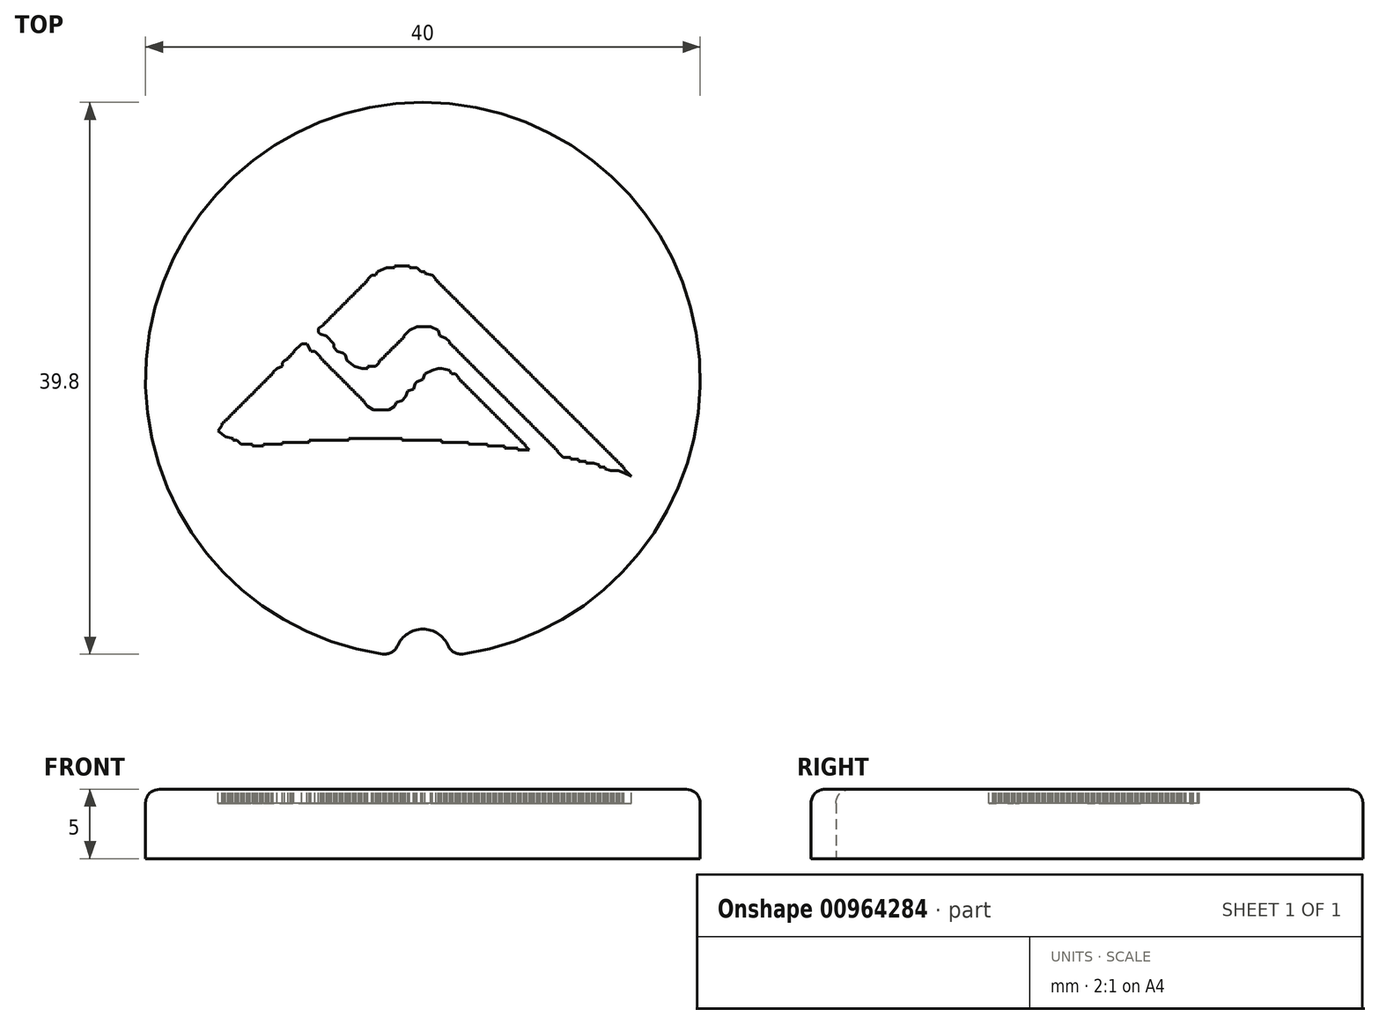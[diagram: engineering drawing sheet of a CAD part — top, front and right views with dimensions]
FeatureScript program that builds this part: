
annotation { "Feature Type Name" : "Feature", "Feature Type Description" : "" }
export const myFeature = defineFeature(function(context is Context, id is Id, definition is map)
    precondition{}
    {
        {
            var Q0;
            Q0=qCreatedBy(makeId("Front.planeOp"),FACE);
            var sketch = newSketch(context, id + "F0", { "sketchPlane" : qUnion([Q0])});
            skLineSegment(sketch, "E0.bottom", {"start": v(0, 0) * mm, "end": v(-20, 0) * mm});
            skLineSegment(sketch, "E0.top", {"start": v(0, 5) * mm, "end": v(-20, 5) * mm});
            skLineSegment(sketch, "E0.left", {"start": v(0, 0) * mm, "end": v(0, 5) * mm});
            skLineSegment(sketch, "E0.right", {"start": v(-20, 0) * mm, "end": v(-20, 5) * mm});
            skSolve(sketch);
        }
        {
            var Q0;
            Q0=qSketchRegion(id+"F0",true);
            var Q1;
            Q1=sQuery(id+"F0.wireOp",EDGE,"E0.left");
            revolve(context, id + "F1", {"surfaceOperationType" : NewSurfaceOperationType.NEW, "entities" : qUnion([Q0]), "axis" : qUnion([Q1]), "revolveType" : RevolveType.FULL});
        }
        {
            var Q0;
            Q0=qCreatedBy(makeId("Top.planeOp"),FACE);
            var sketch = newSketch(context, id + "F2", { "sketchPlane" : qUnion([Q0])});
            skLineSegment(sketch, "E1", {"start": v(0, 0) * mm, "end": v(0, -20) * mm});
            skCircle(sketch, "E2", {"center": v(0, -20) * mm, "radius": 2 * mm});
            skSolve(sketch);
        }
        {
            var Q0;
            Q0=qSketchRegion(id+"F2",true);
            extrude(context, id + "F3", {"entities" : qUnion([Q0]), "operationType" : NewBodyOperationType.REMOVE, "depth" : 25 * mm, "offsetDistance" : 25 * mm});
        }
        {
            var Q0;
            Q0=makeQuery(id+"F1.opRevolve","SWEPT_EDGE",EDGE,{"disambiguationData":[OSD([sQuery(id+"F0.wireOp",EDGE,"E0.top"),sQuery(id+"F0.wireOp",EDGE,"E0.right")])]});
            fillet(context, id + "F4", {"entities" : qUnion([Q0]), "radius" : 1 * mm, "tangentPropagation" : true, "allowEdgeOverflow" : false});
        }
        {
            var Q0;
            Q0=makeQuery(id+"F3.boolean.opBoolean","INTERSECT",EDGE,{"derivedFrom":[makeQuery(id+"F1.opRevolve","SWEPT_FACE",FACE,{"disambiguationData":[OSD([sQuery(id+"F0.wireOp",EDGE,"E0.top")])]}),makeQuery(id+"F3.opExtrude","SWEPT_FACE",FACE,{"disambiguationData":[OSD([sQuery(id+"F2.wireOp",EDGE,"E2")])]})]});
            fillet(context, id + "F5", {"entities" : qUnion([Q0]), "radius" : 1 * mm, "tangentPropagation" : true, "allowEdgeOverflow" : false});
        }
        {
            var Q0;
            Q0=qCreatedBy(makeId("Top.planeOp"),FACE);
            cPlane(context, id + "F6", {"entities" : qUnion([Q0]), "cplaneType" : CPlaneType.OFFSET, "offset" : 5 * mm, "width" : 150 * mm, "height" : 150 * mm});
        }
        {
            var Q0;
            Q0=qCreatedBy(id+"F6.planeOp",FACE);
            var sketch = newSketch(context, id + "F7", { "sketchPlane" : qUnion([Q0])});
            skLineSegment(sketch, "E3", {"start": v(-2.05, 8.2) * mm, "end": v(-2.05, 8.07) * mm});
            skLineSegment(sketch, "E4", {"start": v(-2.05, 8.07) * mm, "end": v(-2.6, 8.07) * mm});
            skLineSegment(sketch, "E5", {"start": v(-2.6, 8.07) * mm, "end": v(-3.28, 7.8) * mm});
            skLineSegment(sketch, "E6", {"start": v(-3.28, 7.8) * mm, "end": v(-3.42, 7.52) * mm});
            skLineSegment(sketch, "E7", {"start": v(-3.42, 7.52) * mm, "end": v(-3.7, 7.52) * mm});
            skLineSegment(sketch, "E8", {"start": v(-3.7, 7.52) * mm, "end": v(-3.97, 7.25) * mm});
            skLineSegment(sketch, "E9", {"start": v(-3.97, 7.25) * mm, "end": v(-3.97, 7.11) * mm});
            skLineSegment(sketch, "E10", {"start": v(-3.97, 7.11) * mm, "end": v(-4.1, 7.11) * mm});
            skLineSegment(sketch, "E11", {"start": v(-4.1, 7.11) * mm, "end": v(-4.1, 6.98) * mm});
            skLineSegment(sketch, "E12", {"start": v(-4.1, 6.98) * mm, "end": v(-4.24, 6.98) * mm});
            skLineSegment(sketch, "E13", {"start": v(-4.24, 6.98) * mm, "end": v(-4.24, 6.84) * mm});
            skLineSegment(sketch, "E14", {"start": v(-4.24, 6.84) * mm, "end": v(-4.38, 6.84) * mm});
            skLineSegment(sketch, "E15", {"start": v(-4.38, 6.84) * mm, "end": v(-4.38, 6.7) * mm});
            skLineSegment(sketch, "E16", {"start": v(-4.38, 6.7) * mm, "end": v(-4.51, 6.7) * mm});
            skLineSegment(sketch, "E17", {"start": v(-4.51, 6.7) * mm, "end": v(-4.51, 6.57) * mm});
            skLineSegment(sketch, "E18", {"start": v(-4.51, 6.57) * mm, "end": v(-4.65, 6.57) * mm});
            skLineSegment(sketch, "E19", {"start": v(-4.65, 6.57) * mm, "end": v(-4.65, 6.43) * mm});
            skLineSegment(sketch, "E20", {"start": v(-4.65, 6.43) * mm, "end": v(-4.79, 6.43) * mm});
            skLineSegment(sketch, "E21", {"start": v(-4.79, 6.43) * mm, "end": v(-4.79, 6.3) * mm});
            skLineSegment(sketch, "E22", {"start": v(-4.79, 6.3) * mm, "end": v(-4.92, 6.3) * mm});
            skLineSegment(sketch, "E23", {"start": v(-4.92, 6.3) * mm, "end": v(-4.92, 6.16) * mm});
            skLineSegment(sketch, "E24", {"start": v(-4.92, 6.16) * mm, "end": v(-5.06, 6.16) * mm});
            skLineSegment(sketch, "E25", {"start": v(-5.06, 6.16) * mm, "end": v(-5.06, 6.02) * mm});
            skLineSegment(sketch, "E26", {"start": v(-5.06, 6.02) * mm, "end": v(-5.2, 6.02) * mm});
            skLineSegment(sketch, "E27", {"start": v(-5.2, 6.02) * mm, "end": v(-5.2, 5.88) * mm});
            skLineSegment(sketch, "E28", {"start": v(-5.2, 5.88) * mm, "end": v(-5.33, 5.88) * mm});
            skLineSegment(sketch, "E29", {"start": v(-5.33, 5.88) * mm, "end": v(-5.33, 5.75) * mm});
            skLineSegment(sketch, "E30", {"start": v(-5.33, 5.75) * mm, "end": v(-5.47, 5.75) * mm});
            skLineSegment(sketch, "E31", {"start": v(-5.47, 5.75) * mm, "end": v(-5.47, 5.6) * mm});
            skLineSegment(sketch, "E32", {"start": v(-5.47, 5.6) * mm, "end": v(-5.6, 5.6) * mm});
            skLineSegment(sketch, "E33", {"start": v(-5.6, 5.6) * mm, "end": v(-5.6, 5.47) * mm});
            skLineSegment(sketch, "E34", {"start": v(-5.6, 5.47) * mm, "end": v(-5.75, 5.47) * mm});
            skLineSegment(sketch, "E35", {"start": v(-5.75, 5.47) * mm, "end": v(-5.75, 5.33) * mm});
            skLineSegment(sketch, "E36", {"start": v(-5.75, 5.33) * mm, "end": v(-5.88, 5.33) * mm});
            skLineSegment(sketch, "E37", {"start": v(-5.88, 5.33) * mm, "end": v(-5.88, 5.2) * mm});
            skLineSegment(sketch, "E38", {"start": v(-5.88, 5.2) * mm, "end": v(-6.02, 5.2) * mm});
            skLineSegment(sketch, "E39", {"start": v(-6.02, 5.2) * mm, "end": v(-6.02, 5.06) * mm});
            skLineSegment(sketch, "E40", {"start": v(-6.02, 5.06) * mm, "end": v(-6.16, 5.06) * mm});
            skLineSegment(sketch, "E41", {"start": v(-6.16, 5.06) * mm, "end": v(-6.16, 4.92) * mm});
            skLineSegment(sketch, "E42", {"start": v(-6.16, 4.92) * mm, "end": v(-6.3, 4.92) * mm});
            skLineSegment(sketch, "E43", {"start": v(-6.3, 4.92) * mm, "end": v(-6.3, 4.79) * mm});
            skLineSegment(sketch, "E44", {"start": v(-6.3, 4.79) * mm, "end": v(-6.43, 4.79) * mm});
            skLineSegment(sketch, "E45", {"start": v(-6.43, 4.79) * mm, "end": v(-6.43, 4.65) * mm});
            skLineSegment(sketch, "E46", {"start": v(-6.43, 4.65) * mm, "end": v(-6.57, 4.65) * mm});
            skLineSegment(sketch, "E47", {"start": v(-6.57, 4.65) * mm, "end": v(-6.57, 4.51) * mm});
            skLineSegment(sketch, "E48", {"start": v(-6.57, 4.51) * mm, "end": v(-6.7, 4.51) * mm});
            skLineSegment(sketch, "E49", {"start": v(-6.7, 4.51) * mm, "end": v(-6.7, 4.38) * mm});
            skLineSegment(sketch, "E50", {"start": v(-6.7, 4.38) * mm, "end": v(-6.84, 4.38) * mm});
            skLineSegment(sketch, "E51", {"start": v(-6.84, 4.38) * mm, "end": v(-6.84, 4.24) * mm});
            skLineSegment(sketch, "E52", {"start": v(-6.84, 4.24) * mm, "end": v(-6.98, 4.24) * mm});
            skLineSegment(sketch, "E53", {"start": v(-6.98, 4.24) * mm, "end": v(-6.98, 4.1) * mm});
            skLineSegment(sketch, "E54", {"start": v(-6.98, 4.1) * mm, "end": v(-7.11, 4.1) * mm});
            skLineSegment(sketch, "E55", {"start": v(-7.11, 4.1) * mm, "end": v(-7.11, 3.97) * mm});
            skLineSegment(sketch, "E56", {"start": v(-7.11, 3.97) * mm, "end": v(-7.52, 3.7) * mm});
            skLineSegment(sketch, "E57", {"start": v(-7.52, 3.7) * mm, "end": v(-7.52, 3.42) * mm});
            skLineSegment(sketch, "E58", {"start": v(-7.52, 3.42) * mm, "end": v(-7.39, 3.28) * mm});
            skLineSegment(sketch, "E59", {"start": v(-7.39, 3.28) * mm, "end": v(-6.98, 3.15) * mm});
            skLineSegment(sketch, "E60", {"start": v(-6.98, 3.15) * mm, "end": v(-6.57, 2.74) * mm});
            skLineSegment(sketch, "E61", {"start": v(-6.57, 2.74) * mm, "end": v(-6.43, 2.6) * mm});
            skLineSegment(sketch, "E62", {"start": v(-6.43, 2.6) * mm, "end": v(-6.43, 2.33) * mm});
            skLineSegment(sketch, "E63", {"start": v(-6.43, 2.33) * mm, "end": v(-6.16, 2.05) * mm});
            skLineSegment(sketch, "E64", {"start": v(-6.16, 2.05) * mm, "end": v(-5.75, 1.92) * mm});
            skLineSegment(sketch, "E65", {"start": v(-5.75, 1.92) * mm, "end": v(-5.6, 1.78) * mm});
            skLineSegment(sketch, "E66", {"start": v(-5.6, 1.78) * mm, "end": v(-5.47, 1.37) * mm});
            skLineSegment(sketch, "E67", {"start": v(-5.47, 1.37) * mm, "end": v(-4.92, 0.96) * mm});
            skLineSegment(sketch, "E68", {"start": v(-4.92, 0.96) * mm, "end": v(-4.38, 0.82) * mm});
            skLineSegment(sketch, "E69", {"start": v(-4.38, 0.82) * mm, "end": v(-3.97, 0.82) * mm});
            skLineSegment(sketch, "E70", {"start": v(-3.97, 0.82) * mm, "end": v(-3.97, 0.96) * mm});
            skLineSegment(sketch, "E71", {"start": v(-3.97, 0.96) * mm, "end": v(-3.42, 0.96) * mm});
            skLineSegment(sketch, "E72", {"start": v(-3.42, 0.96) * mm, "end": v(-3.15, 1.23) * mm});
            skLineSegment(sketch, "E73", {"start": v(-3.15, 1.23) * mm, "end": v(-3.15, 1.37) * mm});
            skLineSegment(sketch, "E74", {"start": v(-3.15, 1.37) * mm, "end": v(-3, 1.37) * mm});
            skLineSegment(sketch, "E75", {"start": v(-3, 1.37) * mm, "end": v(-3, 1.5) * mm});
            skLineSegment(sketch, "E76", {"start": v(-3, 1.5) * mm, "end": v(-2.87, 1.5) * mm});
            skLineSegment(sketch, "E77", {"start": v(-2.87, 1.5) * mm, "end": v(-2.87, 1.64) * mm});
            skLineSegment(sketch, "E78", {"start": v(-2.87, 1.64) * mm, "end": v(-2.74, 1.64) * mm});
            skLineSegment(sketch, "E79", {"start": v(-2.74, 1.64) * mm, "end": v(-2.74, 1.78) * mm});
            skLineSegment(sketch, "E80", {"start": v(-2.74, 1.78) * mm, "end": v(-2.6, 1.78) * mm});
            skLineSegment(sketch, "E81", {"start": v(-2.6, 1.78) * mm, "end": v(-2.6, 1.92) * mm});
            skLineSegment(sketch, "E82", {"start": v(-2.6, 1.92) * mm, "end": v(-2.46, 1.92) * mm});
            skLineSegment(sketch, "E83", {"start": v(-2.46, 1.92) * mm, "end": v(-2.46, 2.05) * mm});
            skLineSegment(sketch, "E84", {"start": v(-2.46, 2.05) * mm, "end": v(-2.33, 2.05) * mm});
            skLineSegment(sketch, "E85", {"start": v(-2.33, 2.05) * mm, "end": v(-2.33, 2.19) * mm});
            skLineSegment(sketch, "E86", {"start": v(-2.33, 2.19) * mm, "end": v(-2.19, 2.19) * mm});
            skLineSegment(sketch, "E87", {"start": v(-2.19, 2.19) * mm, "end": v(-2.19, 2.33) * mm});
            skLineSegment(sketch, "E88", {"start": v(-2.19, 2.33) * mm, "end": v(-2.05, 2.33) * mm});
            skLineSegment(sketch, "E89", {"start": v(-2.05, 2.33) * mm, "end": v(-2.05, 2.46) * mm});
            skLineSegment(sketch, "E90", {"start": v(-2.05, 2.46) * mm, "end": v(-1.92, 2.46) * mm});
            skLineSegment(sketch, "E91", {"start": v(-1.92, 2.46) * mm, "end": v(-1.92, 2.6) * mm});
            skLineSegment(sketch, "E92", {"start": v(-1.92, 2.6) * mm, "end": v(-1.78, 2.6) * mm});
            skLineSegment(sketch, "E93", {"start": v(-1.78, 2.6) * mm, "end": v(-1.78, 2.74) * mm});
            skLineSegment(sketch, "E94", {"start": v(-1.78, 2.74) * mm, "end": v(-1.64, 2.74) * mm});
            skLineSegment(sketch, "E95", {"start": v(-1.64, 2.74) * mm, "end": v(-1.64, 2.87) * mm});
            skLineSegment(sketch, "E96", {"start": v(-1.64, 2.87) * mm, "end": v(-1.5, 2.87) * mm});
            skLineSegment(sketch, "E97", {"start": v(-1.5, 2.87) * mm, "end": v(-1.5, 3) * mm});
            skLineSegment(sketch, "E98", {"start": v(-1.5, 3) * mm, "end": v(-1.37, 3) * mm});
            skLineSegment(sketch, "E99", {"start": v(-1.37, 3) * mm, "end": v(-1.37, 3.15) * mm});
            skLineSegment(sketch, "E100", {"start": v(-1.37, 3.15) * mm, "end": v(-0.96, 3.56) * mm});
            skLineSegment(sketch, "E101", {"start": v(-0.96, 3.56) * mm, "end": v(-0.41, 3.83) * mm});
            skLineSegment(sketch, "E102", {"start": v(-0.41, 3.83) * mm, "end": v(0.55, 3.83) * mm});
            skLineSegment(sketch, "E103", {"start": v(0.55, 3.83) * mm, "end": v(1.1, 3.56) * mm});
            skLineSegment(sketch, "E104", {"start": v(1.1, 3.56) * mm, "end": v(1.23, 3.15) * mm});
            skLineSegment(sketch, "E105", {"start": v(1.23, 3.15) * mm, "end": v(1.64, 3) * mm});
            skLineSegment(sketch, "E106", {"start": v(1.64, 3) * mm, "end": v(1.92, 2.74) * mm});
            skLineSegment(sketch, "E107", {"start": v(1.92, 2.74) * mm, "end": v(1.92, 2.6) * mm});
            skLineSegment(sketch, "E108", {"start": v(1.92, 2.6) * mm, "end": v(2.05, 2.6) * mm});
            skLineSegment(sketch, "E109", {"start": v(2.05, 2.6) * mm, "end": v(2.05, 2.46) * mm});
            skLineSegment(sketch, "E110", {"start": v(2.05, 2.46) * mm, "end": v(2.19, 2.46) * mm});
            skLineSegment(sketch, "E111", {"start": v(2.19, 2.46) * mm, "end": v(2.19, 2.33) * mm});
            skLineSegment(sketch, "E112", {"start": v(2.19, 2.33) * mm, "end": v(2.33, 2.33) * mm});
            skLineSegment(sketch, "E113", {"start": v(2.33, 2.33) * mm, "end": v(2.33, 2.19) * mm});
            skLineSegment(sketch, "E114", {"start": v(2.33, 2.19) * mm, "end": v(2.46, 2.19) * mm});
            skLineSegment(sketch, "E115", {"start": v(2.46, 2.19) * mm, "end": v(2.46, 2.05) * mm});
            skLineSegment(sketch, "E116", {"start": v(2.46, 2.05) * mm, "end": v(2.6, 2.05) * mm});
            skLineSegment(sketch, "E117", {"start": v(2.6, 2.05) * mm, "end": v(2.6, 1.92) * mm});
            skLineSegment(sketch, "E118", {"start": v(2.6, 1.92) * mm, "end": v(2.74, 1.92) * mm});
            skLineSegment(sketch, "E119", {"start": v(2.74, 1.92) * mm, "end": v(2.74, 1.78) * mm});
            skLineSegment(sketch, "E120", {"start": v(2.74, 1.78) * mm, "end": v(2.87, 1.78) * mm});
            skLineSegment(sketch, "E121", {"start": v(2.87, 1.78) * mm, "end": v(2.87, 1.64) * mm});
            skLineSegment(sketch, "E122", {"start": v(2.87, 1.64) * mm, "end": v(3, 1.64) * mm});
            skLineSegment(sketch, "E123", {"start": v(3, 1.64) * mm, "end": v(3, 1.5) * mm});
            skLineSegment(sketch, "E124", {"start": v(3, 1.5) * mm, "end": v(3.15, 1.5) * mm});
            skLineSegment(sketch, "E125", {"start": v(3.15, 1.5) * mm, "end": v(3.15, 1.37) * mm});
            skLineSegment(sketch, "E126", {"start": v(3.15, 1.37) * mm, "end": v(3.28, 1.37) * mm});
            skLineSegment(sketch, "E127", {"start": v(3.28, 1.37) * mm, "end": v(3.28, 1.23) * mm});
            skLineSegment(sketch, "E128", {"start": v(3.28, 1.23) * mm, "end": v(3.42, 1.23) * mm});
            skLineSegment(sketch, "E129", {"start": v(3.42, 1.23) * mm, "end": v(3.42, 1.1) * mm});
            skLineSegment(sketch, "E130", {"start": v(3.42, 1.1) * mm, "end": v(3.56, 1.1) * mm});
            skLineSegment(sketch, "E131", {"start": v(3.56, 1.1) * mm, "end": v(3.56, 0.96) * mm});
            skLineSegment(sketch, "E132", {"start": v(3.56, 0.96) * mm, "end": v(3.7, 0.96) * mm});
            skLineSegment(sketch, "E133", {"start": v(3.7, 0.96) * mm, "end": v(3.7, 0.82) * mm});
            skLineSegment(sketch, "E134", {"start": v(3.7, 0.82) * mm, "end": v(3.83, 0.82) * mm});
            skLineSegment(sketch, "E135", {"start": v(3.83, 0.82) * mm, "end": v(3.83, 0.68) * mm});
            skLineSegment(sketch, "E136", {"start": v(3.83, 0.68) * mm, "end": v(3.97, 0.68) * mm});
            skLineSegment(sketch, "E137", {"start": v(3.97, 0.68) * mm, "end": v(3.97, 0.55) * mm});
            skLineSegment(sketch, "E138", {"start": v(3.97, 0.55) * mm, "end": v(4.1, 0.55) * mm});
            skLineSegment(sketch, "E139", {"start": v(4.1, 0.55) * mm, "end": v(4.1, 0.41) * mm});
            skLineSegment(sketch, "E140", {"start": v(4.1, 0.41) * mm, "end": v(4.24, 0.41) * mm});
            skLineSegment(sketch, "E141", {"start": v(4.24, 0.41) * mm, "end": v(4.24, 0.27) * mm});
            skLineSegment(sketch, "E142", {"start": v(4.24, 0.27) * mm, "end": v(4.38, 0.27) * mm});
            skLineSegment(sketch, "E143", {"start": v(4.38, 0.27) * mm, "end": v(4.38, 0.14) * mm});
            skLineSegment(sketch, "E144", {"start": v(4.38, 0.14) * mm, "end": v(4.51, 0.14) * mm});
            skLineSegment(sketch, "E145", {"start": v(4.51, 0.14) * mm, "end": v(4.51, 0) * mm});
            skLineSegment(sketch, "E146", {"start": v(4.51, 0) * mm, "end": v(4.65, 0) * mm});
            skLineSegment(sketch, "E147", {"start": v(4.65, 0) * mm, "end": v(4.65, -0.14) * mm});
            skLineSegment(sketch, "E148", {"start": v(4.65, -0.14) * mm, "end": v(4.79, -0.14) * mm});
            skLineSegment(sketch, "E149", {"start": v(4.79, -0.14) * mm, "end": v(4.79, -0.27) * mm});
            skLineSegment(sketch, "E150", {"start": v(4.79, -0.27) * mm, "end": v(4.92, -0.27) * mm});
            skLineSegment(sketch, "E151", {"start": v(4.92, -0.27) * mm, "end": v(4.92, -0.41) * mm});
            skLineSegment(sketch, "E152", {"start": v(4.92, -0.41) * mm, "end": v(5.06, -0.41) * mm});
            skLineSegment(sketch, "E153", {"start": v(5.06, -0.41) * mm, "end": v(5.06, -0.55) * mm});
            skLineSegment(sketch, "E154", {"start": v(5.06, -0.55) * mm, "end": v(5.2, -0.55) * mm});
            skLineSegment(sketch, "E155", {"start": v(5.2, -0.55) * mm, "end": v(5.2, -0.68) * mm});
            skLineSegment(sketch, "E156", {"start": v(5.2, -0.68) * mm, "end": v(5.33, -0.68) * mm});
            skLineSegment(sketch, "E157", {"start": v(5.33, -0.68) * mm, "end": v(5.33, -0.82) * mm});
            skLineSegment(sketch, "E158", {"start": v(5.33, -0.82) * mm, "end": v(5.47, -0.82) * mm});
            skLineSegment(sketch, "E159", {"start": v(5.47, -0.82) * mm, "end": v(5.47, -0.96) * mm});
            skLineSegment(sketch, "E160", {"start": v(5.47, -0.96) * mm, "end": v(5.6, -0.96) * mm});
            skLineSegment(sketch, "E161", {"start": v(5.6, -0.96) * mm, "end": v(5.6, -1.1) * mm});
            skLineSegment(sketch, "E162", {"start": v(5.6, -1.1) * mm, "end": v(5.75, -1.1) * mm});
            skLineSegment(sketch, "E163", {"start": v(5.75, -1.1) * mm, "end": v(5.75, -1.23) * mm});
            skLineSegment(sketch, "E164", {"start": v(5.75, -1.23) * mm, "end": v(5.88, -1.23) * mm});
            skLineSegment(sketch, "E165", {"start": v(5.88, -1.23) * mm, "end": v(5.88, -1.37) * mm});
            skLineSegment(sketch, "E166", {"start": v(5.88, -1.37) * mm, "end": v(6.02, -1.37) * mm});
            skLineSegment(sketch, "E167", {"start": v(6.02, -1.37) * mm, "end": v(6.02, -1.5) * mm});
            skLineSegment(sketch, "E168", {"start": v(6.02, -1.5) * mm, "end": v(6.16, -1.5) * mm});
            skLineSegment(sketch, "E169", {"start": v(6.16, -1.5) * mm, "end": v(6.16, -1.64) * mm});
            skLineSegment(sketch, "E170", {"start": v(6.16, -1.64) * mm, "end": v(6.3, -1.64) * mm});
            skLineSegment(sketch, "E171", {"start": v(6.3, -1.64) * mm, "end": v(6.3, -1.78) * mm});
            skLineSegment(sketch, "E172", {"start": v(6.3, -1.78) * mm, "end": v(6.43, -1.78) * mm});
            skLineSegment(sketch, "E173", {"start": v(6.43, -1.78) * mm, "end": v(6.43, -1.92) * mm});
            skLineSegment(sketch, "E174", {"start": v(6.43, -1.92) * mm, "end": v(6.57, -1.92) * mm});
            skLineSegment(sketch, "E175", {"start": v(6.57, -1.92) * mm, "end": v(6.57, -2.05) * mm});
            skLineSegment(sketch, "E176", {"start": v(6.57, -2.05) * mm, "end": v(6.7, -2.05) * mm});
            skLineSegment(sketch, "E177", {"start": v(6.7, -2.05) * mm, "end": v(6.7, -2.19) * mm});
            skLineSegment(sketch, "E178", {"start": v(6.7, -2.19) * mm, "end": v(6.84, -2.19) * mm});
            skLineSegment(sketch, "E179", {"start": v(6.84, -2.19) * mm, "end": v(6.84, -2.33) * mm});
            skLineSegment(sketch, "E180", {"start": v(6.84, -2.33) * mm, "end": v(6.98, -2.33) * mm});
            skLineSegment(sketch, "E181", {"start": v(6.98, -2.33) * mm, "end": v(6.98, -2.46) * mm});
            skLineSegment(sketch, "E182", {"start": v(6.98, -2.46) * mm, "end": v(7.11, -2.46) * mm});
            skLineSegment(sketch, "E183", {"start": v(7.11, -2.46) * mm, "end": v(7.11, -2.6) * mm});
            skLineSegment(sketch, "E184", {"start": v(7.11, -2.6) * mm, "end": v(7.25, -2.6) * mm});
            skLineSegment(sketch, "E185", {"start": v(7.25, -2.6) * mm, "end": v(7.25, -2.74) * mm});
            skLineSegment(sketch, "E186", {"start": v(7.25, -2.74) * mm, "end": v(7.39, -2.74) * mm});
            skLineSegment(sketch, "E187", {"start": v(7.39, -2.74) * mm, "end": v(7.39, -2.87) * mm});
            skLineSegment(sketch, "E188", {"start": v(7.39, -2.87) * mm, "end": v(7.52, -2.87) * mm});
            skLineSegment(sketch, "E189", {"start": v(7.52, -2.87) * mm, "end": v(7.52, -3) * mm});
            skLineSegment(sketch, "E190", {"start": v(7.52, -3) * mm, "end": v(7.66, -3) * mm});
            skLineSegment(sketch, "E191", {"start": v(7.66, -3) * mm, "end": v(7.66, -3.15) * mm});
            skLineSegment(sketch, "E192", {"start": v(7.66, -3.15) * mm, "end": v(7.8, -3.15) * mm});
            skLineSegment(sketch, "E193", {"start": v(7.8, -3.15) * mm, "end": v(7.8, -3.28) * mm});
            skLineSegment(sketch, "E194", {"start": v(7.8, -3.28) * mm, "end": v(7.93, -3.28) * mm});
            skLineSegment(sketch, "E195", {"start": v(7.93, -3.28) * mm, "end": v(7.93, -3.42) * mm});
            skLineSegment(sketch, "E196", {"start": v(7.93, -3.42) * mm, "end": v(8.07, -3.42) * mm});
            skLineSegment(sketch, "E197", {"start": v(8.07, -3.42) * mm, "end": v(8.07, -3.56) * mm});
            skLineSegment(sketch, "E198", {"start": v(8.07, -3.56) * mm, "end": v(8.2, -3.56) * mm});
            skLineSegment(sketch, "E199", {"start": v(8.2, -3.56) * mm, "end": v(8.2, -3.7) * mm});
            skLineSegment(sketch, "E200", {"start": v(8.2, -3.7) * mm, "end": v(8.34, -3.7) * mm});
            skLineSegment(sketch, "E201", {"start": v(8.34, -3.7) * mm, "end": v(8.34, -3.83) * mm});
            skLineSegment(sketch, "E202", {"start": v(8.34, -3.83) * mm, "end": v(8.48, -3.83) * mm});
            skLineSegment(sketch, "E203", {"start": v(8.48, -3.83) * mm, "end": v(8.48, -3.97) * mm});
            skLineSegment(sketch, "E204", {"start": v(8.48, -3.97) * mm, "end": v(8.62, -3.97) * mm});
            skLineSegment(sketch, "E205", {"start": v(8.62, -3.97) * mm, "end": v(8.62, -4.1) * mm});
            skLineSegment(sketch, "E206", {"start": v(8.62, -4.1) * mm, "end": v(8.75, -4.1) * mm});
            skLineSegment(sketch, "E207", {"start": v(8.75, -4.1) * mm, "end": v(8.75, -4.24) * mm});
            skLineSegment(sketch, "E208", {"start": v(8.75, -4.24) * mm, "end": v(8.9, -4.24) * mm});
            skLineSegment(sketch, "E209", {"start": v(8.9, -4.24) * mm, "end": v(8.9, -4.38) * mm});
            skLineSegment(sketch, "E210", {"start": v(8.9, -4.38) * mm, "end": v(9.03, -4.38) * mm});
            skLineSegment(sketch, "E211", {"start": v(9.03, -4.38) * mm, "end": v(9.03, -4.51) * mm});
            skLineSegment(sketch, "E212", {"start": v(9.03, -4.51) * mm, "end": v(9.16, -4.51) * mm});
            skLineSegment(sketch, "E213", {"start": v(9.16, -4.51) * mm, "end": v(9.16, -4.65) * mm});
            skLineSegment(sketch, "E214", {"start": v(9.16, -4.65) * mm, "end": v(9.3, -4.65) * mm});
            skLineSegment(sketch, "E215", {"start": v(9.3, -4.65) * mm, "end": v(9.3, -4.79) * mm});
            skLineSegment(sketch, "E216", {"start": v(9.3, -4.79) * mm, "end": v(9.44, -4.79) * mm});
            skLineSegment(sketch, "E217", {"start": v(9.44, -4.79) * mm, "end": v(9.44, -4.92) * mm});
            skLineSegment(sketch, "E218", {"start": v(9.44, -4.92) * mm, "end": v(9.58, -4.92) * mm});
            skLineSegment(sketch, "E219", {"start": v(9.58, -4.92) * mm, "end": v(9.58, -5.06) * mm});
            skLineSegment(sketch, "E220", {"start": v(9.58, -5.06) * mm, "end": v(9.71, -5.06) * mm});
            skLineSegment(sketch, "E221", {"start": v(9.71, -5.06) * mm, "end": v(9.71, -5.2) * mm});
            skLineSegment(sketch, "E222", {"start": v(9.71, -5.2) * mm, "end": v(10.12, -5.6) * mm});
            skLineSegment(sketch, "E223", {"start": v(10.12, -5.6) * mm, "end": v(10.67, -5.6) * mm});
            skLineSegment(sketch, "E224", {"start": v(10.67, -5.6) * mm, "end": v(10.67, -5.75) * mm});
            skLineSegment(sketch, "E225", {"start": v(10.67, -5.75) * mm, "end": v(11.22, -5.75) * mm});
            skLineSegment(sketch, "E226", {"start": v(11.22, -5.75) * mm, "end": v(11.22, -5.88) * mm});
            skLineSegment(sketch, "E227", {"start": v(11.22, -5.88) * mm, "end": v(11.76, -5.88) * mm});
            skLineSegment(sketch, "E228", {"start": v(11.76, -5.88) * mm, "end": v(11.76, -6.02) * mm});
            skLineSegment(sketch, "E229", {"start": v(11.76, -6.02) * mm, "end": v(12.31, -6.02) * mm});
            skLineSegment(sketch, "E230", {"start": v(12.31, -6.02) * mm, "end": v(12.72, -6.16) * mm});
            skLineSegment(sketch, "E231", {"start": v(12.72, -6.16) * mm, "end": v(12.72, -6.3) * mm});
            skLineSegment(sketch, "E232", {"start": v(12.72, -6.3) * mm, "end": v(13.13, -6.3) * mm});
            skLineSegment(sketch, "E233", {"start": v(13.13, -6.3) * mm, "end": v(13.13, -6.43) * mm});
            skLineSegment(sketch, "E234", {"start": v(13.13, -6.43) * mm, "end": v(13.54, -6.57) * mm});
            skLineSegment(sketch, "E235", {"start": v(13.54, -6.57) * mm, "end": v(14.09, -6.57) * mm});
            skLineSegment(sketch, "E236", {"start": v(14.09, -6.57) * mm, "end": v(14.5, -6.7) * mm});
            skLineSegment(sketch, "E237", {"start": v(14.5, -6.7) * mm, "end": v(15.05, -6.98) * mm});
            skLineSegment(sketch, "E238", {"start": v(15.05, -6.98) * mm, "end": v(14.77, -6.7) * mm});
            skLineSegment(sketch, "E239", {"start": v(14.77, -6.7) * mm, "end": v(14.64, -6.57) * mm});
            skLineSegment(sketch, "E240", {"start": v(14.64, -6.57) * mm, "end": v(14.5, -6.43) * mm});
            skLineSegment(sketch, "E241", {"start": v(14.5, -6.43) * mm, "end": v(14.5, -6.3) * mm});
            skLineSegment(sketch, "E242", {"start": v(14.5, -6.3) * mm, "end": v(14.36, -6.3) * mm});
            skLineSegment(sketch, "E243", {"start": v(14.36, -6.3) * mm, "end": v(14.36, -6.16) * mm});
            skLineSegment(sketch, "E244", {"start": v(14.36, -6.16) * mm, "end": v(14.23, -6.16) * mm});
            skLineSegment(sketch, "E245", {"start": v(14.23, -6.16) * mm, "end": v(14.23, -6.02) * mm});
            skLineSegment(sketch, "E246", {"start": v(14.23, -6.02) * mm, "end": v(14.09, -6.02) * mm});
            skLineSegment(sketch, "E247", {"start": v(14.09, -6.02) * mm, "end": v(14.09, -5.88) * mm});
            skLineSegment(sketch, "E248", {"start": v(14.09, -5.88) * mm, "end": v(13.95, -5.88) * mm});
            skLineSegment(sketch, "E249", {"start": v(13.95, -5.88) * mm, "end": v(13.95, -5.75) * mm});
            skLineSegment(sketch, "E250", {"start": v(13.95, -5.75) * mm, "end": v(13.82, -5.75) * mm});
            skLineSegment(sketch, "E251", {"start": v(13.82, -5.75) * mm, "end": v(13.82, -5.6) * mm});
            skLineSegment(sketch, "E252", {"start": v(13.82, -5.6) * mm, "end": v(13.68, -5.6) * mm});
            skLineSegment(sketch, "E253", {"start": v(13.68, -5.6) * mm, "end": v(13.68, -5.47) * mm});
            skLineSegment(sketch, "E254", {"start": v(13.68, -5.47) * mm, "end": v(13.54, -5.47) * mm});
            skLineSegment(sketch, "E255", {"start": v(13.54, -5.47) * mm, "end": v(13.54, -5.33) * mm});
            skLineSegment(sketch, "E256", {"start": v(13.54, -5.33) * mm, "end": v(13.4, -5.33) * mm});
            skLineSegment(sketch, "E257", {"start": v(13.4, -5.33) * mm, "end": v(13.4, -5.2) * mm});
            skLineSegment(sketch, "E258", {"start": v(13.4, -5.2) * mm, "end": v(13.27, -5.2) * mm});
            skLineSegment(sketch, "E259", {"start": v(13.27, -5.2) * mm, "end": v(13.27, -5.06) * mm});
            skLineSegment(sketch, "E260", {"start": v(13.27, -5.06) * mm, "end": v(13.13, -5.06) * mm});
            skLineSegment(sketch, "E261", {"start": v(13.13, -5.06) * mm, "end": v(13.13, -4.92) * mm});
            skLineSegment(sketch, "E262", {"start": v(13.13, -4.92) * mm, "end": v(13, -4.92) * mm});
            skLineSegment(sketch, "E263", {"start": v(13, -4.92) * mm, "end": v(13, -4.79) * mm});
            skLineSegment(sketch, "E264", {"start": v(13, -4.79) * mm, "end": v(12.86, -4.79) * mm});
            skLineSegment(sketch, "E265", {"start": v(12.86, -4.79) * mm, "end": v(12.86, -4.65) * mm});
            skLineSegment(sketch, "E266", {"start": v(12.86, -4.65) * mm, "end": v(12.72, -4.65) * mm});
            skLineSegment(sketch, "E267", {"start": v(12.72, -4.65) * mm, "end": v(12.72, -4.51) * mm});
            skLineSegment(sketch, "E268", {"start": v(12.72, -4.51) * mm, "end": v(12.58, -4.51) * mm});
            skLineSegment(sketch, "E269", {"start": v(12.58, -4.51) * mm, "end": v(12.58, -4.38) * mm});
            skLineSegment(sketch, "E270", {"start": v(12.58, -4.38) * mm, "end": v(12.45, -4.38) * mm});
            skLineSegment(sketch, "E271", {"start": v(12.45, -4.38) * mm, "end": v(12.45, -4.24) * mm});
            skLineSegment(sketch, "E272", {"start": v(12.45, -4.24) * mm, "end": v(12.31, -4.24) * mm});
            skLineSegment(sketch, "E273", {"start": v(12.31, -4.24) * mm, "end": v(12.31, -4.1) * mm});
            skLineSegment(sketch, "E274", {"start": v(12.31, -4.1) * mm, "end": v(12.17, -4.1) * mm});
            skLineSegment(sketch, "E275", {"start": v(12.17, -4.1) * mm, "end": v(12.17, -3.97) * mm});
            skLineSegment(sketch, "E276", {"start": v(12.17, -3.97) * mm, "end": v(12.04, -3.97) * mm});
            skLineSegment(sketch, "E277", {"start": v(12.04, -3.97) * mm, "end": v(12.04, -3.83) * mm});
            skLineSegment(sketch, "E278", {"start": v(12.04, -3.83) * mm, "end": v(11.9, -3.83) * mm});
            skLineSegment(sketch, "E279", {"start": v(11.9, -3.83) * mm, "end": v(11.9, -3.7) * mm});
            skLineSegment(sketch, "E280", {"start": v(11.9, -3.7) * mm, "end": v(11.76, -3.7) * mm});
            skLineSegment(sketch, "E281", {"start": v(11.76, -3.7) * mm, "end": v(11.76, -3.56) * mm});
            skLineSegment(sketch, "E282", {"start": v(11.76, -3.56) * mm, "end": v(11.63, -3.56) * mm});
            skLineSegment(sketch, "E283", {"start": v(11.63, -3.56) * mm, "end": v(11.63, -3.42) * mm});
            skLineSegment(sketch, "E284", {"start": v(11.63, -3.42) * mm, "end": v(11.5, -3.42) * mm});
            skLineSegment(sketch, "E285", {"start": v(11.5, -3.42) * mm, "end": v(11.5, -3.28) * mm});
            skLineSegment(sketch, "E286", {"start": v(11.5, -3.28) * mm, "end": v(11.35, -3.28) * mm});
            skLineSegment(sketch, "E287", {"start": v(11.35, -3.28) * mm, "end": v(11.35, -3.15) * mm});
            skLineSegment(sketch, "E288", {"start": v(11.35, -3.15) * mm, "end": v(11.22, -3.15) * mm});
            skLineSegment(sketch, "E289", {"start": v(11.22, -3.15) * mm, "end": v(11.22, -3) * mm});
            skLineSegment(sketch, "E290", {"start": v(11.22, -3) * mm, "end": v(11.08, -3) * mm});
            skLineSegment(sketch, "E291", {"start": v(11.08, -3) * mm, "end": v(11.08, -2.87) * mm});
            skLineSegment(sketch, "E292", {"start": v(11.08, -2.87) * mm, "end": v(10.94, -2.87) * mm});
            skLineSegment(sketch, "E293", {"start": v(10.94, -2.87) * mm, "end": v(10.94, -2.74) * mm});
            skLineSegment(sketch, "E294", {"start": v(10.94, -2.74) * mm, "end": v(10.8, -2.74) * mm});
            skLineSegment(sketch, "E295", {"start": v(10.8, -2.74) * mm, "end": v(10.8, -2.6) * mm});
            skLineSegment(sketch, "E296", {"start": v(10.8, -2.6) * mm, "end": v(10.67, -2.6) * mm});
            skLineSegment(sketch, "E297", {"start": v(10.67, -2.6) * mm, "end": v(10.67, -2.46) * mm});
            skLineSegment(sketch, "E298", {"start": v(10.67, -2.46) * mm, "end": v(10.53, -2.46) * mm});
            skLineSegment(sketch, "E299", {"start": v(10.53, -2.46) * mm, "end": v(10.53, -2.33) * mm});
            skLineSegment(sketch, "E300", {"start": v(10.53, -2.33) * mm, "end": v(10.4, -2.33) * mm});
            skLineSegment(sketch, "E301", {"start": v(10.4, -2.33) * mm, "end": v(10.4, -2.19) * mm});
            skLineSegment(sketch, "E302", {"start": v(10.4, -2.19) * mm, "end": v(10.26, -2.19) * mm});
            skLineSegment(sketch, "E303", {"start": v(10.26, -2.19) * mm, "end": v(10.26, -2.05) * mm});
            skLineSegment(sketch, "E304", {"start": v(10.26, -2.05) * mm, "end": v(10.12, -2.05) * mm});
            skLineSegment(sketch, "E305", {"start": v(10.12, -2.05) * mm, "end": v(10.12, -1.92) * mm});
            skLineSegment(sketch, "E306", {"start": v(10.12, -1.92) * mm, "end": v(9.99, -1.92) * mm});
            skLineSegment(sketch, "E307", {"start": v(9.99, -1.92) * mm, "end": v(9.99, -1.78) * mm});
            skLineSegment(sketch, "E308", {"start": v(9.99, -1.78) * mm, "end": v(9.85, -1.78) * mm});
            skLineSegment(sketch, "E309", {"start": v(9.85, -1.78) * mm, "end": v(9.85, -1.64) * mm});
            skLineSegment(sketch, "E310", {"start": v(9.85, -1.64) * mm, "end": v(9.71, -1.64) * mm});
            skLineSegment(sketch, "E311", {"start": v(9.71, -1.64) * mm, "end": v(9.71, -1.5) * mm});
            skLineSegment(sketch, "E312", {"start": v(9.71, -1.5) * mm, "end": v(9.58, -1.5) * mm});
            skLineSegment(sketch, "E313", {"start": v(9.58, -1.5) * mm, "end": v(9.58, -1.37) * mm});
            skLineSegment(sketch, "E314", {"start": v(9.58, -1.37) * mm, "end": v(9.44, -1.37) * mm});
            skLineSegment(sketch, "E315", {"start": v(9.44, -1.37) * mm, "end": v(9.44, -1.23) * mm});
            skLineSegment(sketch, "E316", {"start": v(9.44, -1.23) * mm, "end": v(9.3, -1.23) * mm});
            skLineSegment(sketch, "E317", {"start": v(9.3, -1.23) * mm, "end": v(9.3, -1.1) * mm});
            skLineSegment(sketch, "E318", {"start": v(9.3, -1.1) * mm, "end": v(9.16, -1.1) * mm});
            skLineSegment(sketch, "E319", {"start": v(9.16, -1.1) * mm, "end": v(9.16, -0.96) * mm});
            skLineSegment(sketch, "E320", {"start": v(9.16, -0.96) * mm, "end": v(9.03, -0.96) * mm});
            skLineSegment(sketch, "E321", {"start": v(9.03, -0.96) * mm, "end": v(9.03, -0.82) * mm});
            skLineSegment(sketch, "E322", {"start": v(9.03, -0.82) * mm, "end": v(8.9, -0.82) * mm});
            skLineSegment(sketch, "E323", {"start": v(8.9, -0.82) * mm, "end": v(8.9, -0.68) * mm});
            skLineSegment(sketch, "E324", {"start": v(8.9, -0.68) * mm, "end": v(8.75, -0.68) * mm});
            skLineSegment(sketch, "E325", {"start": v(8.75, -0.68) * mm, "end": v(8.75, -0.55) * mm});
            skLineSegment(sketch, "E326", {"start": v(8.75, -0.55) * mm, "end": v(8.62, -0.55) * mm});
            skLineSegment(sketch, "E327", {"start": v(8.62, -0.55) * mm, "end": v(8.62, -0.41) * mm});
            skLineSegment(sketch, "E328", {"start": v(8.62, -0.41) * mm, "end": v(8.48, -0.41) * mm});
            skLineSegment(sketch, "E329", {"start": v(8.48, -0.41) * mm, "end": v(8.48, -0.27) * mm});
            skLineSegment(sketch, "E330", {"start": v(8.48, -0.27) * mm, "end": v(8.34, -0.27) * mm});
            skLineSegment(sketch, "E331", {"start": v(8.34, -0.27) * mm, "end": v(8.34, -0.14) * mm});
            skLineSegment(sketch, "E332", {"start": v(8.34, -0.14) * mm, "end": v(8.2, -0.14) * mm});
            skLineSegment(sketch, "E333", {"start": v(8.2, -0.14) * mm, "end": v(8.2, 0) * mm});
            skLineSegment(sketch, "E334", {"start": v(8.2, 0) * mm, "end": v(8.07, 0) * mm});
            skLineSegment(sketch, "E335", {"start": v(8.07, 0) * mm, "end": v(8.07, 0.14) * mm});
            skLineSegment(sketch, "E336", {"start": v(8.07, 0.14) * mm, "end": v(7.93, 0.14) * mm});
            skLineSegment(sketch, "E337", {"start": v(7.93, 0.14) * mm, "end": v(7.93, 0.27) * mm});
            skLineSegment(sketch, "E338", {"start": v(7.93, 0.27) * mm, "end": v(7.8, 0.27) * mm});
            skLineSegment(sketch, "E339", {"start": v(7.8, 0.27) * mm, "end": v(7.8, 0.41) * mm});
            skLineSegment(sketch, "E340", {"start": v(7.8, 0.41) * mm, "end": v(7.66, 0.41) * mm});
            skLineSegment(sketch, "E341", {"start": v(7.66, 0.41) * mm, "end": v(7.66, 0.55) * mm});
            skLineSegment(sketch, "E342", {"start": v(7.66, 0.55) * mm, "end": v(7.52, 0.55) * mm});
            skLineSegment(sketch, "E343", {"start": v(7.52, 0.55) * mm, "end": v(7.52, 0.68) * mm});
            skLineSegment(sketch, "E344", {"start": v(7.52, 0.68) * mm, "end": v(7.39, 0.68) * mm});
            skLineSegment(sketch, "E345", {"start": v(7.39, 0.68) * mm, "end": v(7.39, 0.82) * mm});
            skLineSegment(sketch, "E346", {"start": v(7.39, 0.82) * mm, "end": v(7.25, 0.82) * mm});
            skLineSegment(sketch, "E347", {"start": v(7.25, 0.82) * mm, "end": v(7.25, 0.96) * mm});
            skLineSegment(sketch, "E348", {"start": v(7.25, 0.96) * mm, "end": v(7.11, 0.96) * mm});
            skLineSegment(sketch, "E349", {"start": v(7.11, 0.96) * mm, "end": v(7.11, 1.1) * mm});
            skLineSegment(sketch, "E350", {"start": v(7.11, 1.1) * mm, "end": v(6.98, 1.1) * mm});
            skLineSegment(sketch, "E351", {"start": v(6.98, 1.1) * mm, "end": v(6.98, 1.23) * mm});
            skLineSegment(sketch, "E352", {"start": v(6.98, 1.23) * mm, "end": v(6.84, 1.23) * mm});
            skLineSegment(sketch, "E353", {"start": v(6.84, 1.23) * mm, "end": v(6.84, 1.37) * mm});
            skLineSegment(sketch, "E354", {"start": v(6.84, 1.37) * mm, "end": v(6.7, 1.37) * mm});
            skLineSegment(sketch, "E355", {"start": v(6.7, 1.37) * mm, "end": v(6.7, 1.5) * mm});
            skLineSegment(sketch, "E356", {"start": v(6.7, 1.5) * mm, "end": v(6.57, 1.5) * mm});
            skLineSegment(sketch, "E357", {"start": v(6.57, 1.5) * mm, "end": v(6.57, 1.64) * mm});
            skLineSegment(sketch, "E358", {"start": v(6.57, 1.64) * mm, "end": v(6.43, 1.64) * mm});
            skLineSegment(sketch, "E359", {"start": v(6.43, 1.64) * mm, "end": v(6.43, 1.78) * mm});
            skLineSegment(sketch, "E360", {"start": v(6.43, 1.78) * mm, "end": v(6.3, 1.78) * mm});
            skLineSegment(sketch, "E361", {"start": v(6.3, 1.78) * mm, "end": v(6.3, 1.92) * mm});
            skLineSegment(sketch, "E362", {"start": v(6.3, 1.92) * mm, "end": v(6.16, 1.92) * mm});
            skLineSegment(sketch, "E363", {"start": v(6.16, 1.92) * mm, "end": v(6.16, 2.05) * mm});
            skLineSegment(sketch, "E364", {"start": v(6.16, 2.05) * mm, "end": v(6.02, 2.05) * mm});
            skLineSegment(sketch, "E365", {"start": v(6.02, 2.05) * mm, "end": v(6.02, 2.19) * mm});
            skLineSegment(sketch, "E366", {"start": v(6.02, 2.19) * mm, "end": v(5.88, 2.19) * mm});
            skLineSegment(sketch, "E367", {"start": v(5.88, 2.19) * mm, "end": v(5.88, 2.33) * mm});
            skLineSegment(sketch, "E368", {"start": v(5.88, 2.33) * mm, "end": v(5.75, 2.33) * mm});
            skLineSegment(sketch, "E369", {"start": v(5.75, 2.33) * mm, "end": v(5.75, 2.46) * mm});
            skLineSegment(sketch, "E370", {"start": v(5.75, 2.46) * mm, "end": v(5.6, 2.46) * mm});
            skLineSegment(sketch, "E371", {"start": v(5.6, 2.46) * mm, "end": v(5.6, 2.6) * mm});
            skLineSegment(sketch, "E372", {"start": v(5.6, 2.6) * mm, "end": v(5.47, 2.6) * mm});
            skLineSegment(sketch, "E373", {"start": v(5.47, 2.6) * mm, "end": v(5.47, 2.74) * mm});
            skLineSegment(sketch, "E374", {"start": v(5.47, 2.74) * mm, "end": v(5.33, 2.74) * mm});
            skLineSegment(sketch, "E375", {"start": v(5.33, 2.74) * mm, "end": v(5.33, 2.87) * mm});
            skLineSegment(sketch, "E376", {"start": v(5.33, 2.87) * mm, "end": v(5.2, 2.87) * mm});
            skLineSegment(sketch, "E377", {"start": v(5.2, 2.87) * mm, "end": v(5.2, 3) * mm});
            skLineSegment(sketch, "E378", {"start": v(5.2, 3) * mm, "end": v(5.06, 3) * mm});
            skLineSegment(sketch, "E379", {"start": v(5.06, 3) * mm, "end": v(5.06, 3.15) * mm});
            skLineSegment(sketch, "E380", {"start": v(5.06, 3.15) * mm, "end": v(4.92, 3.15) * mm});
            skLineSegment(sketch, "E381", {"start": v(4.92, 3.15) * mm, "end": v(4.92, 3.28) * mm});
            skLineSegment(sketch, "E382", {"start": v(4.92, 3.28) * mm, "end": v(4.79, 3.28) * mm});
            skLineSegment(sketch, "E383", {"start": v(4.79, 3.28) * mm, "end": v(4.79, 3.42) * mm});
            skLineSegment(sketch, "E384", {"start": v(4.79, 3.42) * mm, "end": v(4.65, 3.42) * mm});
            skLineSegment(sketch, "E385", {"start": v(4.65, 3.42) * mm, "end": v(4.65, 3.56) * mm});
            skLineSegment(sketch, "E386", {"start": v(4.65, 3.56) * mm, "end": v(4.51, 3.56) * mm});
            skLineSegment(sketch, "E387", {"start": v(4.51, 3.56) * mm, "end": v(4.51, 3.7) * mm});
            skLineSegment(sketch, "E388", {"start": v(4.51, 3.7) * mm, "end": v(4.38, 3.7) * mm});
            skLineSegment(sketch, "E389", {"start": v(4.38, 3.7) * mm, "end": v(4.38, 3.83) * mm});
            skLineSegment(sketch, "E390", {"start": v(4.38, 3.83) * mm, "end": v(4.24, 3.83) * mm});
            skLineSegment(sketch, "E391", {"start": v(4.24, 3.83) * mm, "end": v(4.24, 3.97) * mm});
            skLineSegment(sketch, "E392", {"start": v(4.24, 3.97) * mm, "end": v(4.1, 3.97) * mm});
            skLineSegment(sketch, "E393", {"start": v(4.1, 3.97) * mm, "end": v(4.1, 4.1) * mm});
            skLineSegment(sketch, "E394", {"start": v(4.1, 4.1) * mm, "end": v(3.97, 4.1) * mm});
            skLineSegment(sketch, "E395", {"start": v(3.97, 4.1) * mm, "end": v(3.97, 4.24) * mm});
            skLineSegment(sketch, "E396", {"start": v(3.97, 4.24) * mm, "end": v(3.83, 4.24) * mm});
            skLineSegment(sketch, "E397", {"start": v(3.83, 4.24) * mm, "end": v(3.83, 4.38) * mm});
            skLineSegment(sketch, "E398", {"start": v(3.83, 4.38) * mm, "end": v(3.7, 4.38) * mm});
            skLineSegment(sketch, "E399", {"start": v(3.7, 4.38) * mm, "end": v(3.7, 4.51) * mm});
            skLineSegment(sketch, "E400", {"start": v(3.7, 4.51) * mm, "end": v(3.56, 4.51) * mm});
            skLineSegment(sketch, "E401", {"start": v(3.56, 4.51) * mm, "end": v(3.56, 4.65) * mm});
            skLineSegment(sketch, "E402", {"start": v(3.56, 4.65) * mm, "end": v(3.42, 4.65) * mm});
            skLineSegment(sketch, "E403", {"start": v(3.42, 4.65) * mm, "end": v(3.42, 4.79) * mm});
            skLineSegment(sketch, "E404", {"start": v(3.42, 4.79) * mm, "end": v(3.28, 4.79) * mm});
            skLineSegment(sketch, "E405", {"start": v(3.28, 4.79) * mm, "end": v(3.28, 4.92) * mm});
            skLineSegment(sketch, "E406", {"start": v(3.28, 4.92) * mm, "end": v(3.15, 4.92) * mm});
            skLineSegment(sketch, "E407", {"start": v(3.15, 4.92) * mm, "end": v(3.15, 5.06) * mm});
            skLineSegment(sketch, "E408", {"start": v(3.15, 5.06) * mm, "end": v(3, 5.06) * mm});
            skLineSegment(sketch, "E409", {"start": v(3, 5.06) * mm, "end": v(3, 5.2) * mm});
            skLineSegment(sketch, "E410", {"start": v(3, 5.2) * mm, "end": v(2.87, 5.2) * mm});
            skLineSegment(sketch, "E411", {"start": v(2.87, 5.2) * mm, "end": v(2.87, 5.33) * mm});
            skLineSegment(sketch, "E412", {"start": v(2.87, 5.33) * mm, "end": v(2.74, 5.33) * mm});
            skLineSegment(sketch, "E413", {"start": v(2.74, 5.33) * mm, "end": v(2.74, 5.47) * mm});
            skLineSegment(sketch, "E414", {"start": v(2.74, 5.47) * mm, "end": v(2.6, 5.47) * mm});
            skLineSegment(sketch, "E415", {"start": v(2.6, 5.47) * mm, "end": v(2.6, 5.6) * mm});
            skLineSegment(sketch, "E416", {"start": v(2.6, 5.6) * mm, "end": v(2.46, 5.6) * mm});
            skLineSegment(sketch, "E417", {"start": v(2.46, 5.6) * mm, "end": v(2.46, 5.75) * mm});
            skLineSegment(sketch, "E418", {"start": v(2.46, 5.75) * mm, "end": v(2.33, 5.75) * mm});
            skLineSegment(sketch, "E419", {"start": v(2.33, 5.75) * mm, "end": v(2.33, 5.88) * mm});
            skLineSegment(sketch, "E420", {"start": v(2.33, 5.88) * mm, "end": v(2.19, 5.88) * mm});
            skLineSegment(sketch, "E421", {"start": v(2.19, 5.88) * mm, "end": v(2.19, 6.02) * mm});
            skLineSegment(sketch, "E422", {"start": v(2.19, 6.02) * mm, "end": v(2.05, 6.02) * mm});
            skLineSegment(sketch, "E423", {"start": v(2.05, 6.02) * mm, "end": v(2.05, 6.16) * mm});
            skLineSegment(sketch, "E424", {"start": v(2.05, 6.16) * mm, "end": v(1.92, 6.16) * mm});
            skLineSegment(sketch, "E425", {"start": v(1.92, 6.16) * mm, "end": v(1.92, 6.3) * mm});
            skLineSegment(sketch, "E426", {"start": v(1.92, 6.3) * mm, "end": v(1.78, 6.3) * mm});
            skLineSegment(sketch, "E427", {"start": v(1.78, 6.3) * mm, "end": v(1.78, 6.43) * mm});
            skLineSegment(sketch, "E428", {"start": v(1.78, 6.43) * mm, "end": v(1.64, 6.43) * mm});
            skLineSegment(sketch, "E429", {"start": v(1.64, 6.43) * mm, "end": v(1.64, 6.57) * mm});
            skLineSegment(sketch, "E430", {"start": v(1.64, 6.57) * mm, "end": v(1.5, 6.57) * mm});
            skLineSegment(sketch, "E431", {"start": v(1.5, 6.57) * mm, "end": v(1.5, 6.7) * mm});
            skLineSegment(sketch, "E432", {"start": v(1.5, 6.7) * mm, "end": v(1.37, 6.7) * mm});
            skLineSegment(sketch, "E433", {"start": v(1.37, 6.7) * mm, "end": v(1.37, 6.84) * mm});
            skLineSegment(sketch, "E434", {"start": v(1.37, 6.84) * mm, "end": v(1.23, 6.84) * mm});
            skLineSegment(sketch, "E435", {"start": v(1.23, 6.84) * mm, "end": v(1.23, 6.98) * mm});
            skLineSegment(sketch, "E436", {"start": v(1.23, 6.98) * mm, "end": v(1.1, 6.98) * mm});
            skLineSegment(sketch, "E437", {"start": v(1.1, 6.98) * mm, "end": v(1.1, 7.11) * mm});
            skLineSegment(sketch, "E438", {"start": v(1.1, 7.11) * mm, "end": v(0.96, 7.11) * mm});
            skLineSegment(sketch, "E439", {"start": v(0.96, 7.11) * mm, "end": v(0.96, 7.25) * mm});
            skLineSegment(sketch, "E440", {"start": v(0.96, 7.25) * mm, "end": v(0.68, 7.52) * mm});
            skLineSegment(sketch, "E441", {"start": v(0.68, 7.52) * mm, "end": v(0.14, 7.66) * mm});
            skLineSegment(sketch, "E442", {"start": v(0.14, 7.66) * mm, "end": v(0.14, 7.8) * mm});
            skLineSegment(sketch, "E443", {"start": v(0.14, 7.8) * mm, "end": v(-0.14, 7.8) * mm});
            skLineSegment(sketch, "E444", {"start": v(-0.14, 7.8) * mm, "end": v(-0.41, 8.07) * mm});
            skLineSegment(sketch, "E445", {"start": v(-0.41, 8.07) * mm, "end": v(-0.96, 8.07) * mm});
            skLineSegment(sketch, "E446", {"start": v(-0.96, 8.07) * mm, "end": v(-0.96, 8.2) * mm});
            skLineSegment(sketch, "E447", {"start": v(-0.96, 8.2) * mm, "end": v(-2.05, 8.2) * mm});
            skLineSegment(sketch, "E448", {"start": v(-8.75, 2.6) * mm, "end": v(-9.03, 2.33) * mm});
            skLineSegment(sketch, "E449", {"start": v(-9.03, 2.33) * mm, "end": v(-9.16, 2.19) * mm});
            skLineSegment(sketch, "E450", {"start": v(-9.16, 2.19) * mm, "end": v(-9.3, 2.05) * mm});
            skLineSegment(sketch, "E451", {"start": v(-9.3, 2.05) * mm, "end": v(-9.3, 1.92) * mm});
            skLineSegment(sketch, "E452", {"start": v(-9.3, 1.92) * mm, "end": v(-9.44, 1.92) * mm});
            skLineSegment(sketch, "E453", {"start": v(-9.44, 1.92) * mm, "end": v(-9.44, 1.78) * mm});
            skLineSegment(sketch, "E454", {"start": v(-9.44, 1.78) * mm, "end": v(-9.58, 1.78) * mm});
            skLineSegment(sketch, "E455", {"start": v(-9.58, 1.78) * mm, "end": v(-9.58, 1.64) * mm});
            skLineSegment(sketch, "E456", {"start": v(-9.58, 1.64) * mm, "end": v(-9.71, 1.64) * mm});
            skLineSegment(sketch, "E457", {"start": v(-9.71, 1.64) * mm, "end": v(-9.71, 1.5) * mm});
            skLineSegment(sketch, "E458", {"start": v(-9.71, 1.5) * mm, "end": v(-9.99, 1.37) * mm});
            skLineSegment(sketch, "E459", {"start": v(-9.99, 1.37) * mm, "end": v(-10.12, 1.23) * mm});
            skLineSegment(sketch, "E460", {"start": v(-10.12, 1.23) * mm, "end": v(-10.12, 0.96) * mm});
            skLineSegment(sketch, "E461", {"start": v(-10.12, 0.96) * mm, "end": v(-10.53, 0.82) * mm});
            skLineSegment(sketch, "E462", {"start": v(-10.53, 0.82) * mm, "end": v(-10.8, 0.55) * mm});
            skLineSegment(sketch, "E463", {"start": v(-10.8, 0.55) * mm, "end": v(-10.8, 0.41) * mm});
            skLineSegment(sketch, "E464", {"start": v(-10.8, 0.41) * mm, "end": v(-10.94, 0.41) * mm});
            skLineSegment(sketch, "E465", {"start": v(-10.94, 0.41) * mm, "end": v(-10.94, 0.27) * mm});
            skLineSegment(sketch, "E466", {"start": v(-10.94, 0.27) * mm, "end": v(-11.08, 0.27) * mm});
            skLineSegment(sketch, "E467", {"start": v(-11.08, 0.27) * mm, "end": v(-11.08, 0.14) * mm});
            skLineSegment(sketch, "E468", {"start": v(-11.08, 0.14) * mm, "end": v(-11.22, 0.14) * mm});
            skLineSegment(sketch, "E469", {"start": v(-11.22, 0.14) * mm, "end": v(-11.22, 0) * mm});
            skLineSegment(sketch, "E470", {"start": v(-11.22, 0) * mm, "end": v(-11.35, 0) * mm});
            skLineSegment(sketch, "E471", {"start": v(-11.35, 0) * mm, "end": v(-11.35, -0.14) * mm});
            skLineSegment(sketch, "E472", {"start": v(-11.35, -0.14) * mm, "end": v(-11.5, -0.14) * mm});
            skLineSegment(sketch, "E473", {"start": v(-11.5, -0.14) * mm, "end": v(-11.5, -0.27) * mm});
            skLineSegment(sketch, "E474", {"start": v(-11.5, -0.27) * mm, "end": v(-11.63, -0.27) * mm});
            skLineSegment(sketch, "E475", {"start": v(-11.63, -0.27) * mm, "end": v(-11.63, -0.41) * mm});
            skLineSegment(sketch, "E476", {"start": v(-11.63, -0.41) * mm, "end": v(-11.76, -0.41) * mm});
            skLineSegment(sketch, "E477", {"start": v(-11.76, -0.41) * mm, "end": v(-11.76, -0.55) * mm});
            skLineSegment(sketch, "E478", {"start": v(-11.76, -0.55) * mm, "end": v(-11.9, -0.55) * mm});
            skLineSegment(sketch, "E479", {"start": v(-11.9, -0.55) * mm, "end": v(-11.9, -0.68) * mm});
            skLineSegment(sketch, "E480", {"start": v(-11.9, -0.68) * mm, "end": v(-12.04, -0.68) * mm});
            skLineSegment(sketch, "E481", {"start": v(-12.04, -0.68) * mm, "end": v(-12.04, -0.82) * mm});
            skLineSegment(sketch, "E482", {"start": v(-12.04, -0.82) * mm, "end": v(-12.17, -0.82) * mm});
            skLineSegment(sketch, "E483", {"start": v(-12.17, -0.82) * mm, "end": v(-12.17, -0.96) * mm});
            skLineSegment(sketch, "E484", {"start": v(-12.17, -0.96) * mm, "end": v(-12.31, -0.96) * mm});
            skLineSegment(sketch, "E485", {"start": v(-12.31, -0.96) * mm, "end": v(-12.31, -1.1) * mm});
            skLineSegment(sketch, "E486", {"start": v(-12.31, -1.1) * mm, "end": v(-12.45, -1.1) * mm});
            skLineSegment(sketch, "E487", {"start": v(-12.45, -1.1) * mm, "end": v(-12.45, -1.23) * mm});
            skLineSegment(sketch, "E488", {"start": v(-12.45, -1.23) * mm, "end": v(-12.58, -1.23) * mm});
            skLineSegment(sketch, "E489", {"start": v(-12.58, -1.23) * mm, "end": v(-12.58, -1.37) * mm});
            skLineSegment(sketch, "E490", {"start": v(-12.58, -1.37) * mm, "end": v(-12.72, -1.37) * mm});
            skLineSegment(sketch, "E491", {"start": v(-12.72, -1.37) * mm, "end": v(-12.72, -1.5) * mm});
            skLineSegment(sketch, "E492", {"start": v(-12.72, -1.5) * mm, "end": v(-12.86, -1.5) * mm});
            skLineSegment(sketch, "E493", {"start": v(-12.86, -1.5) * mm, "end": v(-12.86, -1.64) * mm});
            skLineSegment(sketch, "E494", {"start": v(-12.86, -1.64) * mm, "end": v(-13, -1.64) * mm});
            skLineSegment(sketch, "E495", {"start": v(-13, -1.64) * mm, "end": v(-13, -1.78) * mm});
            skLineSegment(sketch, "E496", {"start": v(-13, -1.78) * mm, "end": v(-13.13, -1.78) * mm});
            skLineSegment(sketch, "E497", {"start": v(-13.13, -1.78) * mm, "end": v(-13.13, -1.92) * mm});
            skLineSegment(sketch, "E498", {"start": v(-13.13, -1.92) * mm, "end": v(-13.27, -1.92) * mm});
            skLineSegment(sketch, "E499", {"start": v(-13.27, -1.92) * mm, "end": v(-13.27, -2.05) * mm});
            skLineSegment(sketch, "E500", {"start": v(-13.27, -2.05) * mm, "end": v(-13.4, -2.05) * mm});
            skLineSegment(sketch, "E501", {"start": v(-13.4, -2.05) * mm, "end": v(-13.4, -2.19) * mm});
            skLineSegment(sketch, "E502", {"start": v(-13.4, -2.19) * mm, "end": v(-13.54, -2.19) * mm});
            skLineSegment(sketch, "E503", {"start": v(-13.54, -2.19) * mm, "end": v(-13.54, -2.33) * mm});
            skLineSegment(sketch, "E504", {"start": v(-13.54, -2.33) * mm, "end": v(-13.68, -2.33) * mm});
            skLineSegment(sketch, "E505", {"start": v(-13.68, -2.33) * mm, "end": v(-13.68, -2.46) * mm});
            skLineSegment(sketch, "E506", {"start": v(-13.68, -2.46) * mm, "end": v(-13.82, -2.46) * mm});
            skLineSegment(sketch, "E507", {"start": v(-13.82, -2.46) * mm, "end": v(-13.82, -2.6) * mm});
            skLineSegment(sketch, "E508", {"start": v(-13.82, -2.6) * mm, "end": v(-13.95, -2.6) * mm});
            skLineSegment(sketch, "E509", {"start": v(-13.95, -2.6) * mm, "end": v(-13.95, -2.74) * mm});
            skLineSegment(sketch, "E510", {"start": v(-13.95, -2.74) * mm, "end": v(-14.09, -2.74) * mm});
            skLineSegment(sketch, "E511", {"start": v(-14.09, -2.74) * mm, "end": v(-14.09, -2.87) * mm});
            skLineSegment(sketch, "E512", {"start": v(-14.09, -2.87) * mm, "end": v(-14.23, -2.87) * mm});
            skLineSegment(sketch, "E513", {"start": v(-14.23, -2.87) * mm, "end": v(-14.23, -3) * mm});
            skLineSegment(sketch, "E514", {"start": v(-14.23, -3) * mm, "end": v(-14.36, -3) * mm});
            skLineSegment(sketch, "E515", {"start": v(-14.36, -3) * mm, "end": v(-14.36, -3.15) * mm});
            skLineSegment(sketch, "E516", {"start": v(-14.36, -3.15) * mm, "end": v(-14.5, -3.15) * mm});
            skLineSegment(sketch, "E517", {"start": v(-14.5, -3.15) * mm, "end": v(-14.5, -3.28) * mm});
            skLineSegment(sketch, "E518", {"start": v(-14.5, -3.28) * mm, "end": v(-14.77, -3.7) * mm});
            skLineSegment(sketch, "E519", {"start": v(-14.77, -3.7) * mm, "end": v(-14.23, -4.1) * mm});
            skLineSegment(sketch, "E520", {"start": v(-14.23, -4.1) * mm, "end": v(-13.68, -4.24) * mm});
            skLineSegment(sketch, "E521", {"start": v(-13.68, -4.24) * mm, "end": v(-13.68, -4.38) * mm});
            skLineSegment(sketch, "E522", {"start": v(-13.68, -4.38) * mm, "end": v(-13.4, -4.38) * mm});
            skLineSegment(sketch, "E523", {"start": v(-13.4, -4.38) * mm, "end": v(-13.13, -4.65) * mm});
            skLineSegment(sketch, "E524", {"start": v(-13.13, -4.65) * mm, "end": v(-12.31, -4.65) * mm});
            skLineSegment(sketch, "E525", {"start": v(-12.31, -4.65) * mm, "end": v(-12.31, -4.79) * mm});
            skLineSegment(sketch, "E526", {"start": v(-12.31, -4.79) * mm, "end": v(-11.5, -4.79) * mm});
            skLineSegment(sketch, "E527", {"start": v(-11.5, -4.79) * mm, "end": v(-11.5, -4.65) * mm});
            skLineSegment(sketch, "E528", {"start": v(-11.5, -4.65) * mm, "end": v(-11.08, -4.65) * mm});
            skLineSegment(sketch, "E529", {"start": v(-11.08, -4.65) * mm, "end": v(-10.12, -4.65) * mm});
            skLineSegment(sketch, "E530", {"start": v(-10.12, -4.65) * mm, "end": v(-10.12, -4.51) * mm});
            skLineSegment(sketch, "E531", {"start": v(-10.12, -4.51) * mm, "end": v(-9.71, -4.51) * mm});
            skLineSegment(sketch, "E532", {"start": v(-9.71, -4.51) * mm, "end": v(-9.16, -4.51) * mm});
            skLineSegment(sketch, "E533", {"start": v(-9.16, -4.51) * mm, "end": v(-9.03, -4.51) * mm});
            skLineSegment(sketch, "E534", {"start": v(-9.03, -4.51) * mm, "end": v(-8.9, -4.51) * mm});
            skLineSegment(sketch, "E535", {"start": v(-8.9, -4.51) * mm, "end": v(-8.75, -4.51) * mm});
            skLineSegment(sketch, "E536", {"start": v(-8.75, -4.51) * mm, "end": v(-8.2, -4.51) * mm});
            skLineSegment(sketch, "E537", {"start": v(-8.2, -4.51) * mm, "end": v(-8.2, -4.38) * mm});
            skLineSegment(sketch, "E538", {"start": v(-8.2, -4.38) * mm, "end": v(-7.8, -4.38) * mm});
            skLineSegment(sketch, "E539", {"start": v(-7.8, -4.38) * mm, "end": v(-7.25, -4.38) * mm});
            skLineSegment(sketch, "E540", {"start": v(-7.25, -4.38) * mm, "end": v(-7.11, -4.38) * mm});
            skLineSegment(sketch, "E541", {"start": v(-7.11, -4.38) * mm, "end": v(-6.98, -4.38) * mm});
            skLineSegment(sketch, "E542", {"start": v(-6.98, -4.38) * mm, "end": v(-6.84, -4.38) * mm});
            skLineSegment(sketch, "E543", {"start": v(-6.84, -4.38) * mm, "end": v(-6.7, -4.38) * mm});
            skLineSegment(sketch, "E544", {"start": v(-6.7, -4.38) * mm, "end": v(-6.57, -4.38) * mm});
            skLineSegment(sketch, "E545", {"start": v(-6.57, -4.38) * mm, "end": v(-6.43, -4.38) * mm});
            skLineSegment(sketch, "E546", {"start": v(-6.43, -4.38) * mm, "end": v(-6.3, -4.38) * mm});
            skLineSegment(sketch, "E547", {"start": v(-6.3, -4.38) * mm, "end": v(-5.33, -4.38) * mm});
            skLineSegment(sketch, "E548", {"start": v(-5.33, -4.38) * mm, "end": v(-5.33, -4.24) * mm});
            skLineSegment(sketch, "E549", {"start": v(-5.33, -4.24) * mm, "end": v(-4.92, -4.24) * mm});
            skLineSegment(sketch, "E550", {"start": v(-4.92, -4.24) * mm, "end": v(-4.38, -4.24) * mm});
            skLineSegment(sketch, "E551", {"start": v(-4.38, -4.24) * mm, "end": v(-4.24, -4.24) * mm});
            skLineSegment(sketch, "E552", {"start": v(-4.24, -4.24) * mm, "end": v(-4.1, -4.24) * mm});
            skLineSegment(sketch, "E553", {"start": v(-4.1, -4.24) * mm, "end": v(-3.97, -4.24) * mm});
            skLineSegment(sketch, "E554", {"start": v(-3.97, -4.24) * mm, "end": v(-3.83, -4.24) * mm});
            skLineSegment(sketch, "E555", {"start": v(-3.83, -4.24) * mm, "end": v(-3.7, -4.24) * mm});
            skLineSegment(sketch, "E556", {"start": v(-3.7, -4.24) * mm, "end": v(-3.56, -4.24) * mm});
            skLineSegment(sketch, "E557", {"start": v(-3.56, -4.24) * mm, "end": v(-3.42, -4.24) * mm});
            skLineSegment(sketch, "E558", {"start": v(-3.42, -4.24) * mm, "end": v(-3.28, -4.24) * mm});
            skLineSegment(sketch, "E559", {"start": v(-3.28, -4.24) * mm, "end": v(-3.15, -4.24) * mm});
            skLineSegment(sketch, "E560", {"start": v(-3.15, -4.24) * mm, "end": v(-3, -4.24) * mm});
            skLineSegment(sketch, "E561", {"start": v(-3, -4.24) * mm, "end": v(-2.87, -4.24) * mm});
            skLineSegment(sketch, "E562", {"start": v(-2.87, -4.24) * mm, "end": v(-2.74, -4.24) * mm});
            skLineSegment(sketch, "E563", {"start": v(-2.74, -4.24) * mm, "end": v(-2.6, -4.24) * mm});
            skLineSegment(sketch, "E564", {"start": v(-2.6, -4.24) * mm, "end": v(-2.46, -4.24) * mm});
            skLineSegment(sketch, "E565", {"start": v(-2.46, -4.24) * mm, "end": v(-2.33, -4.24) * mm});
            skLineSegment(sketch, "E566", {"start": v(-2.33, -4.24) * mm, "end": v(-1.5, -4.24) * mm});
            skLineSegment(sketch, "E567", {"start": v(-1.5, -4.24) * mm, "end": v(-1.5, -4.38) * mm});
            skLineSegment(sketch, "E568", {"start": v(-1.5, -4.38) * mm, "end": v(-1.1, -4.38) * mm});
            skLineSegment(sketch, "E569", {"start": v(-1.1, -4.38) * mm, "end": v(-0.55, -4.38) * mm});
            skLineSegment(sketch, "E570", {"start": v(-0.55, -4.38) * mm, "end": v(-0.41, -4.38) * mm});
            skLineSegment(sketch, "E571", {"start": v(-0.41, -4.38) * mm, "end": v(-0.27, -4.38) * mm});
            skLineSegment(sketch, "E572", {"start": v(-0.27, -4.38) * mm, "end": v(-0.14, -4.38) * mm});
            skLineSegment(sketch, "E573", {"start": v(-0.14, -4.38) * mm, "end": v(0, -4.38) * mm});
            skLineSegment(sketch, "E574", {"start": v(0, -4.38) * mm, "end": v(0.14, -4.38) * mm});
            skLineSegment(sketch, "E575", {"start": v(0.14, -4.38) * mm, "end": v(0.27, -4.38) * mm});
            skLineSegment(sketch, "E576", {"start": v(0.27, -4.38) * mm, "end": v(0.41, -4.38) * mm});
            skLineSegment(sketch, "E577", {"start": v(0.41, -4.38) * mm, "end": v(1.37, -4.38) * mm});
            skLineSegment(sketch, "E578", {"start": v(1.37, -4.38) * mm, "end": v(1.37, -4.51) * mm});
            skLineSegment(sketch, "E579", {"start": v(1.37, -4.51) * mm, "end": v(1.78, -4.51) * mm});
            skLineSegment(sketch, "E580", {"start": v(1.78, -4.51) * mm, "end": v(2.33, -4.51) * mm});
            skLineSegment(sketch, "E581", {"start": v(2.33, -4.51) * mm, "end": v(2.46, -4.51) * mm});
            skLineSegment(sketch, "E582", {"start": v(2.46, -4.51) * mm, "end": v(2.6, -4.51) * mm});
            skLineSegment(sketch, "E583", {"start": v(2.6, -4.51) * mm, "end": v(2.74, -4.51) * mm});
            skLineSegment(sketch, "E584", {"start": v(2.74, -4.51) * mm, "end": v(3.28, -4.51) * mm});
            skLineSegment(sketch, "E585", {"start": v(3.28, -4.51) * mm, "end": v(3.28, -4.65) * mm});
            skLineSegment(sketch, "E586", {"start": v(3.28, -4.65) * mm, "end": v(3.7, -4.65) * mm});
            skLineSegment(sketch, "E587", {"start": v(3.7, -4.65) * mm, "end": v(4.65, -4.65) * mm});
            skLineSegment(sketch, "E588", {"start": v(4.65, -4.65) * mm, "end": v(4.65, -4.79) * mm});
            skLineSegment(sketch, "E589", {"start": v(4.65, -4.79) * mm, "end": v(5.06, -4.79) * mm});
            skLineSegment(sketch, "E590", {"start": v(5.06, -4.79) * mm, "end": v(5.47, -4.79) * mm});
            skLineSegment(sketch, "E591", {"start": v(5.47, -4.79) * mm, "end": v(5.88, -4.79) * mm});
            skLineSegment(sketch, "E592", {"start": v(5.88, -4.79) * mm, "end": v(5.88, -4.92) * mm});
            skLineSegment(sketch, "E593", {"start": v(5.88, -4.92) * mm, "end": v(6.84, -4.92) * mm});
            skLineSegment(sketch, "E594", {"start": v(6.84, -4.92) * mm, "end": v(6.84, -5.06) * mm});
            skLineSegment(sketch, "E595", {"start": v(6.84, -5.06) * mm, "end": v(7.66, -5.06) * mm});
            skLineSegment(sketch, "E596", {"start": v(7.66, -5.06) * mm, "end": v(7.39, -4.79) * mm});
            skLineSegment(sketch, "E597", {"start": v(7.39, -4.79) * mm, "end": v(7.39, -4.65) * mm});
            skLineSegment(sketch, "E598", {"start": v(7.39, -4.65) * mm, "end": v(7.25, -4.65) * mm});
            skLineSegment(sketch, "E599", {"start": v(7.25, -4.65) * mm, "end": v(7.25, -4.51) * mm});
            skLineSegment(sketch, "E600", {"start": v(7.25, -4.51) * mm, "end": v(7.11, -4.51) * mm});
            skLineSegment(sketch, "E601", {"start": v(7.11, -4.51) * mm, "end": v(7.11, -4.38) * mm});
            skLineSegment(sketch, "E602", {"start": v(7.11, -4.38) * mm, "end": v(6.98, -4.38) * mm});
            skLineSegment(sketch, "E603", {"start": v(6.98, -4.38) * mm, "end": v(6.98, -4.24) * mm});
            skLineSegment(sketch, "E604", {"start": v(6.98, -4.24) * mm, "end": v(6.84, -4.24) * mm});
            skLineSegment(sketch, "E605", {"start": v(6.84, -4.24) * mm, "end": v(6.84, -4.1) * mm});
            skLineSegment(sketch, "E606", {"start": v(6.84, -4.1) * mm, "end": v(6.7, -4.1) * mm});
            skLineSegment(sketch, "E607", {"start": v(6.7, -4.1) * mm, "end": v(6.7, -3.97) * mm});
            skLineSegment(sketch, "E608", {"start": v(6.7, -3.97) * mm, "end": v(6.57, -3.97) * mm});
            skLineSegment(sketch, "E609", {"start": v(6.57, -3.97) * mm, "end": v(6.57, -3.83) * mm});
            skLineSegment(sketch, "E610", {"start": v(6.57, -3.83) * mm, "end": v(6.43, -3.83) * mm});
            skLineSegment(sketch, "E611", {"start": v(6.43, -3.83) * mm, "end": v(6.43, -3.7) * mm});
            skLineSegment(sketch, "E612", {"start": v(6.43, -3.7) * mm, "end": v(6.3, -3.7) * mm});
            skLineSegment(sketch, "E613", {"start": v(6.3, -3.7) * mm, "end": v(6.3, -3.56) * mm});
            skLineSegment(sketch, "E614", {"start": v(6.3, -3.56) * mm, "end": v(6.16, -3.56) * mm});
            skLineSegment(sketch, "E615", {"start": v(6.16, -3.56) * mm, "end": v(6.16, -3.42) * mm});
            skLineSegment(sketch, "E616", {"start": v(6.16, -3.42) * mm, "end": v(6.02, -3.42) * mm});
            skLineSegment(sketch, "E617", {"start": v(6.02, -3.42) * mm, "end": v(6.02, -3.28) * mm});
            skLineSegment(sketch, "E618", {"start": v(6.02, -3.28) * mm, "end": v(5.88, -3.28) * mm});
            skLineSegment(sketch, "E619", {"start": v(5.88, -3.28) * mm, "end": v(5.88, -3.15) * mm});
            skLineSegment(sketch, "E620", {"start": v(5.88, -3.15) * mm, "end": v(5.75, -3.15) * mm});
            skLineSegment(sketch, "E621", {"start": v(5.75, -3.15) * mm, "end": v(5.75, -3) * mm});
            skLineSegment(sketch, "E622", {"start": v(5.75, -3) * mm, "end": v(5.6, -3) * mm});
            skLineSegment(sketch, "E623", {"start": v(5.6, -3) * mm, "end": v(5.6, -2.87) * mm});
            skLineSegment(sketch, "E624", {"start": v(5.6, -2.87) * mm, "end": v(5.47, -2.87) * mm});
            skLineSegment(sketch, "E625", {"start": v(5.47, -2.87) * mm, "end": v(5.47, -2.74) * mm});
            skLineSegment(sketch, "E626", {"start": v(5.47, -2.74) * mm, "end": v(5.33, -2.74) * mm});
            skLineSegment(sketch, "E627", {"start": v(5.33, -2.74) * mm, "end": v(5.33, -2.6) * mm});
            skLineSegment(sketch, "E628", {"start": v(5.33, -2.6) * mm, "end": v(5.2, -2.6) * mm});
            skLineSegment(sketch, "E629", {"start": v(5.2, -2.6) * mm, "end": v(5.2, -2.46) * mm});
            skLineSegment(sketch, "E630", {"start": v(5.2, -2.46) * mm, "end": v(5.06, -2.46) * mm});
            skLineSegment(sketch, "E631", {"start": v(5.06, -2.46) * mm, "end": v(5.06, -2.33) * mm});
            skLineSegment(sketch, "E632", {"start": v(5.06, -2.33) * mm, "end": v(4.92, -2.33) * mm});
            skLineSegment(sketch, "E633", {"start": v(4.92, -2.33) * mm, "end": v(4.92, -2.19) * mm});
            skLineSegment(sketch, "E634", {"start": v(4.92, -2.19) * mm, "end": v(4.79, -2.19) * mm});
            skLineSegment(sketch, "E635", {"start": v(4.79, -2.19) * mm, "end": v(4.79, -2.05) * mm});
            skLineSegment(sketch, "E636", {"start": v(4.79, -2.05) * mm, "end": v(4.65, -2.05) * mm});
            skLineSegment(sketch, "E637", {"start": v(4.65, -2.05) * mm, "end": v(4.65, -1.92) * mm});
            skLineSegment(sketch, "E638", {"start": v(4.65, -1.92) * mm, "end": v(4.51, -1.92) * mm});
            skLineSegment(sketch, "E639", {"start": v(4.51, -1.92) * mm, "end": v(4.51, -1.78) * mm});
            skLineSegment(sketch, "E640", {"start": v(4.51, -1.78) * mm, "end": v(4.38, -1.78) * mm});
            skLineSegment(sketch, "E641", {"start": v(4.38, -1.78) * mm, "end": v(4.38, -1.64) * mm});
            skLineSegment(sketch, "E642", {"start": v(4.38, -1.64) * mm, "end": v(4.24, -1.64) * mm});
            skLineSegment(sketch, "E643", {"start": v(4.24, -1.64) * mm, "end": v(4.24, -1.5) * mm});
            skLineSegment(sketch, "E644", {"start": v(4.24, -1.5) * mm, "end": v(4.1, -1.5) * mm});
            skLineSegment(sketch, "E645", {"start": v(4.1, -1.5) * mm, "end": v(4.1, -1.37) * mm});
            skLineSegment(sketch, "E646", {"start": v(4.1, -1.37) * mm, "end": v(3.97, -1.37) * mm});
            skLineSegment(sketch, "E647", {"start": v(3.97, -1.37) * mm, "end": v(3.97, -1.23) * mm});
            skLineSegment(sketch, "E648", {"start": v(3.97, -1.23) * mm, "end": v(3.83, -1.23) * mm});
            skLineSegment(sketch, "E649", {"start": v(3.83, -1.23) * mm, "end": v(3.83, -1.1) * mm});
            skLineSegment(sketch, "E650", {"start": v(3.83, -1.1) * mm, "end": v(3.7, -1.1) * mm});
            skLineSegment(sketch, "E651", {"start": v(3.7, -1.1) * mm, "end": v(3.7, -0.96) * mm});
            skLineSegment(sketch, "E652", {"start": v(3.7, -0.96) * mm, "end": v(3.56, -0.96) * mm});
            skLineSegment(sketch, "E653", {"start": v(3.56, -0.96) * mm, "end": v(3.56, -0.82) * mm});
            skLineSegment(sketch, "E654", {"start": v(3.56, -0.82) * mm, "end": v(3.42, -0.82) * mm});
            skLineSegment(sketch, "E655", {"start": v(3.42, -0.82) * mm, "end": v(3.42, -0.68) * mm});
            skLineSegment(sketch, "E656", {"start": v(3.42, -0.68) * mm, "end": v(3.28, -0.68) * mm});
            skLineSegment(sketch, "E657", {"start": v(3.28, -0.68) * mm, "end": v(3.28, -0.55) * mm});
            skLineSegment(sketch, "E658", {"start": v(3.28, -0.55) * mm, "end": v(3.15, -0.55) * mm});
            skLineSegment(sketch, "E659", {"start": v(3.15, -0.55) * mm, "end": v(3.15, -0.41) * mm});
            skLineSegment(sketch, "E660", {"start": v(3.15, -0.41) * mm, "end": v(3, -0.41) * mm});
            skLineSegment(sketch, "E661", {"start": v(3, -0.41) * mm, "end": v(3, -0.27) * mm});
            skLineSegment(sketch, "E662", {"start": v(3, -0.27) * mm, "end": v(2.87, -0.27) * mm});
            skLineSegment(sketch, "E663", {"start": v(2.87, -0.27) * mm, "end": v(2.87, -0.14) * mm});
            skLineSegment(sketch, "E664", {"start": v(2.87, -0.14) * mm, "end": v(2.74, -0.14) * mm});
            skLineSegment(sketch, "E665", {"start": v(2.74, -0.14) * mm, "end": v(2.74, 0) * mm});
            skLineSegment(sketch, "E666", {"start": v(2.74, 0) * mm, "end": v(2.6, 0) * mm});
            skLineSegment(sketch, "E667", {"start": v(2.6, 0) * mm, "end": v(2.6, 0.14) * mm});
            skLineSegment(sketch, "E668", {"start": v(2.6, 0.14) * mm, "end": v(2.33, 0.41) * mm});
            skLineSegment(sketch, "E669", {"start": v(2.33, 0.41) * mm, "end": v(2.05, 0.41) * mm});
            skLineSegment(sketch, "E670", {"start": v(2.05, 0.41) * mm, "end": v(1.92, 0.68) * mm});
            skLineSegment(sketch, "E671", {"start": v(1.92, 0.68) * mm, "end": v(1.37, 0.82) * mm});
            skLineSegment(sketch, "E672", {"start": v(1.37, 0.82) * mm, "end": v(1.1, 0.82) * mm});
            skLineSegment(sketch, "E673", {"start": v(1.1, 0.82) * mm, "end": v(0.68, 0.68) * mm});
            skLineSegment(sketch, "E674", {"start": v(0.68, 0.68) * mm, "end": v(0.14, 0.41) * mm});
            skLineSegment(sketch, "E675", {"start": v(0.14, 0.41) * mm, "end": v(0, 0) * mm});
            skLineSegment(sketch, "E676", {"start": v(0, 0) * mm, "end": v(-0.41, -0.14) * mm});
            skLineSegment(sketch, "E677", {"start": v(-0.41, -0.14) * mm, "end": v(-0.55, -0.27) * mm});
            skLineSegment(sketch, "E678", {"start": v(-0.55, -0.27) * mm, "end": v(-0.68, -0.68) * mm});
            skLineSegment(sketch, "E679", {"start": v(-0.68, -0.68) * mm, "end": v(-1.1, -0.82) * mm});
            skLineSegment(sketch, "E680", {"start": v(-1.1, -0.82) * mm, "end": v(-1.23, -1.23) * mm});
            skLineSegment(sketch, "E681", {"start": v(-1.23, -1.23) * mm, "end": v(-1.5, -1.5) * mm});
            skLineSegment(sketch, "E682", {"start": v(-1.5, -1.5) * mm, "end": v(-1.92, -1.64) * mm});
            skLineSegment(sketch, "E683", {"start": v(-1.92, -1.64) * mm, "end": v(-2.05, -1.92) * mm});
            skLineSegment(sketch, "E684", {"start": v(-2.05, -1.92) * mm, "end": v(-2.46, -2.19) * mm});
            skLineSegment(sketch, "E685", {"start": v(-2.46, -2.19) * mm, "end": v(-3.56, -2.19) * mm});
            skLineSegment(sketch, "E686", {"start": v(-3.56, -2.19) * mm, "end": v(-3.97, -1.92) * mm});
            skLineSegment(sketch, "E687", {"start": v(-3.97, -1.92) * mm, "end": v(-4.24, -1.64) * mm});
            skLineSegment(sketch, "E688", {"start": v(-4.24, -1.64) * mm, "end": v(-4.24, -1.5) * mm});
            skLineSegment(sketch, "E689", {"start": v(-4.24, -1.5) * mm, "end": v(-4.38, -1.5) * mm});
            skLineSegment(sketch, "E690", {"start": v(-4.38, -1.5) * mm, "end": v(-4.38, -1.37) * mm});
            skLineSegment(sketch, "E691", {"start": v(-4.38, -1.37) * mm, "end": v(-4.51, -1.37) * mm});
            skLineSegment(sketch, "E692", {"start": v(-4.51, -1.37) * mm, "end": v(-4.51, -1.23) * mm});
            skLineSegment(sketch, "E693", {"start": v(-4.51, -1.23) * mm, "end": v(-4.65, -1.23) * mm});
            skLineSegment(sketch, "E694", {"start": v(-4.65, -1.23) * mm, "end": v(-4.65, -1.1) * mm});
            skLineSegment(sketch, "E695", {"start": v(-4.65, -1.1) * mm, "end": v(-4.79, -1.1) * mm});
            skLineSegment(sketch, "E696", {"start": v(-4.79, -1.1) * mm, "end": v(-4.79, -0.96) * mm});
            skLineSegment(sketch, "E697", {"start": v(-4.79, -0.96) * mm, "end": v(-4.92, -0.96) * mm});
            skLineSegment(sketch, "E698", {"start": v(-4.92, -0.96) * mm, "end": v(-4.92, -0.82) * mm});
            skLineSegment(sketch, "E699", {"start": v(-4.92, -0.82) * mm, "end": v(-5.06, -0.82) * mm});
            skLineSegment(sketch, "E700", {"start": v(-5.06, -0.82) * mm, "end": v(-5.06, -0.68) * mm});
            skLineSegment(sketch, "E701", {"start": v(-5.06, -0.68) * mm, "end": v(-5.2, -0.68) * mm});
            skLineSegment(sketch, "E702", {"start": v(-5.2, -0.68) * mm, "end": v(-5.2, -0.55) * mm});
            skLineSegment(sketch, "E703", {"start": v(-5.2, -0.55) * mm, "end": v(-5.33, -0.55) * mm});
            skLineSegment(sketch, "E704", {"start": v(-5.33, -0.55) * mm, "end": v(-5.33, -0.41) * mm});
            skLineSegment(sketch, "E705", {"start": v(-5.33, -0.41) * mm, "end": v(-5.47, -0.41) * mm});
            skLineSegment(sketch, "E706", {"start": v(-5.47, -0.41) * mm, "end": v(-5.47, -0.27) * mm});
            skLineSegment(sketch, "E707", {"start": v(-5.47, -0.27) * mm, "end": v(-5.6, -0.27) * mm});
            skLineSegment(sketch, "E708", {"start": v(-5.6, -0.27) * mm, "end": v(-5.6, -0.14) * mm});
            skLineSegment(sketch, "E709", {"start": v(-5.6, -0.14) * mm, "end": v(-5.75, -0.14) * mm});
            skLineSegment(sketch, "E710", {"start": v(-5.75, -0.14) * mm, "end": v(-5.75, 0) * mm});
            skLineSegment(sketch, "E711", {"start": v(-5.75, 0) * mm, "end": v(-5.88, 0) * mm});
            skLineSegment(sketch, "E712", {"start": v(-5.88, 0) * mm, "end": v(-5.88, 0.14) * mm});
            skLineSegment(sketch, "E713", {"start": v(-5.88, 0.14) * mm, "end": v(-6.02, 0.14) * mm});
            skLineSegment(sketch, "E714", {"start": v(-6.02, 0.14) * mm, "end": v(-6.02, 0.27) * mm});
            skLineSegment(sketch, "E715", {"start": v(-6.02, 0.27) * mm, "end": v(-6.16, 0.27) * mm});
            skLineSegment(sketch, "E716", {"start": v(-6.16, 0.27) * mm, "end": v(-6.16, 0.41) * mm});
            skLineSegment(sketch, "E717", {"start": v(-6.16, 0.41) * mm, "end": v(-6.3, 0.41) * mm});
            skLineSegment(sketch, "E718", {"start": v(-6.3, 0.41) * mm, "end": v(-6.3, 0.55) * mm});
            skLineSegment(sketch, "E719", {"start": v(-6.3, 0.55) * mm, "end": v(-6.43, 0.55) * mm});
            skLineSegment(sketch, "E720", {"start": v(-6.43, 0.55) * mm, "end": v(-6.43, 0.68) * mm});
            skLineSegment(sketch, "E721", {"start": v(-6.43, 0.68) * mm, "end": v(-6.57, 0.68) * mm});
            skLineSegment(sketch, "E722", {"start": v(-6.57, 0.68) * mm, "end": v(-6.57, 0.82) * mm});
            skLineSegment(sketch, "E723", {"start": v(-6.57, 0.82) * mm, "end": v(-6.7, 0.82) * mm});
            skLineSegment(sketch, "E724", {"start": v(-6.7, 0.82) * mm, "end": v(-6.7, 0.96) * mm});
            skLineSegment(sketch, "E725", {"start": v(-6.7, 0.96) * mm, "end": v(-6.84, 0.96) * mm});
            skLineSegment(sketch, "E726", {"start": v(-6.84, 0.96) * mm, "end": v(-6.84, 1.1) * mm});
            skLineSegment(sketch, "E727", {"start": v(-6.84, 1.1) * mm, "end": v(-6.98, 1.1) * mm});
            skLineSegment(sketch, "E728", {"start": v(-6.98, 1.1) * mm, "end": v(-6.98, 1.23) * mm});
            skLineSegment(sketch, "E729", {"start": v(-6.98, 1.23) * mm, "end": v(-7.11, 1.23) * mm});
            skLineSegment(sketch, "E730", {"start": v(-7.11, 1.23) * mm, "end": v(-7.11, 1.37) * mm});
            skLineSegment(sketch, "E731", {"start": v(-7.11, 1.37) * mm, "end": v(-7.25, 1.37) * mm});
            skLineSegment(sketch, "E732", {"start": v(-7.25, 1.37) * mm, "end": v(-7.25, 1.5) * mm});
            skLineSegment(sketch, "E733", {"start": v(-7.25, 1.5) * mm, "end": v(-7.39, 1.5) * mm});
            skLineSegment(sketch, "E734", {"start": v(-7.39, 1.5) * mm, "end": v(-7.39, 1.64) * mm});
            skLineSegment(sketch, "E735", {"start": v(-7.39, 1.64) * mm, "end": v(-7.66, 1.92) * mm});
            skLineSegment(sketch, "E736", {"start": v(-7.66, 1.92) * mm, "end": v(-7.8, 2.05) * mm});
            skLineSegment(sketch, "E737", {"start": v(-7.8, 2.05) * mm, "end": v(-8.07, 2.05) * mm});
            skLineSegment(sketch, "E738", {"start": v(-8.07, 2.05) * mm, "end": v(-8.34, 2.6) * mm});
            skLineSegment(sketch, "E739", {"start": v(-8.34, 2.6) * mm, "end": v(-8.75, 2.6) * mm});
            skSolve(sketch);
        }
        {
            var Q0;
            Q0 = qSketchRegion(id + "F7", true);
            extrude(context, id + "F8", {"entities" : qUnion([Q0]), "operationType" : NewBodyOperationType.REMOVE, "oppositeDirection" : true, "depth" : 1 * mm, "offsetDistance" : 25 * mm});
        }
    });
